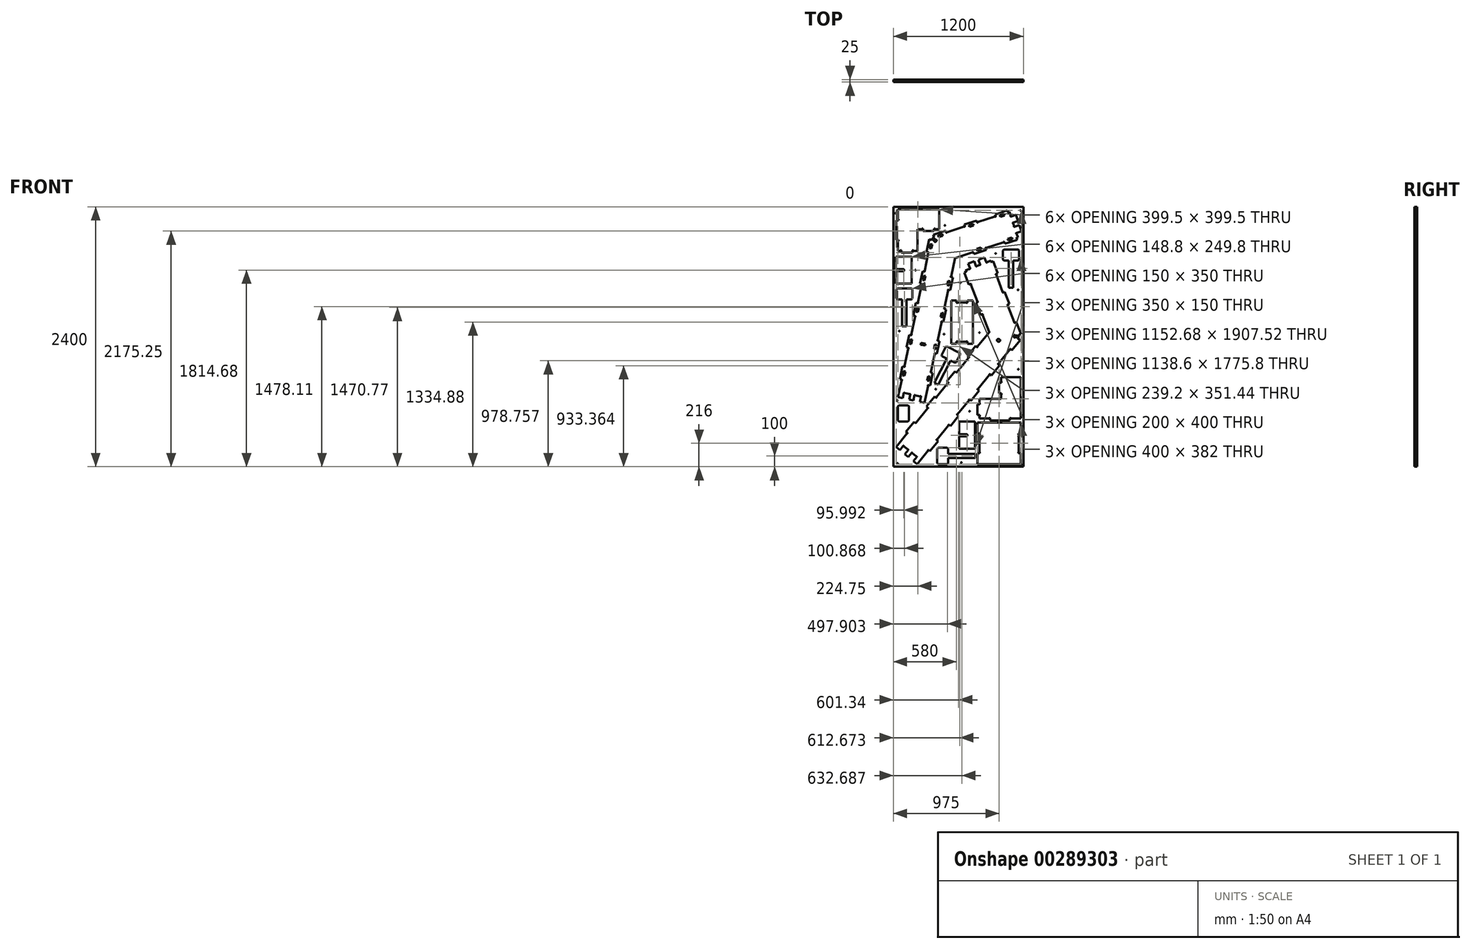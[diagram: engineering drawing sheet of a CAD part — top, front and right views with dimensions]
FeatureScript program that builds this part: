
annotation { "Feature Type Name" : "Feature", "Feature Type Description" : "" }
export const myFeature = defineFeature(function(context is Context, id is Id, definition is map)
    precondition{}
    {
        {
            var Q0;
            Q0=qCreatedBy(makeId("Front.planeOp"),FACE);
            var sketch = newSketch(context, id + "F0", { "sketchPlane" : qUnion([Q0])});
            skLineSegment(sketch, "E0", {"start": v(-600, -1200) * mm, "end": v(600, -1200) * mm});
            skLineSegment(sketch, "E1", {"start": v(600, -1200) * mm, "end": v(600, 1200) * mm});
            skLineSegment(sketch, "E2", {"start": v(600, 1200) * mm, "end": v(-600, 1200) * mm});
            skLineSegment(sketch, "E3", {"start": v(-600, 1200) * mm, "end": v(-600, -1200) * mm});
            skLineSegment(sketch, "E4", {"start": v(-525, 775.5) * mm, "end": v(-525, 798.5) * mm});
            skLineSegment(sketch, "E5", {"start": v(-525, 798.5) * mm, "end": v(-535.5, 798.5) * mm});
            skLineSegment(sketch, "E6", {"start": v(-535.5, 798.5) * mm, "end": v(-535.5, 793.5) * mm});
            skLineSegment(sketch, "E7", {"start": v(-535.5, 793.5) * mm, "end": v(-557, 793.5) * mm});
            skLineSegment(sketch, "E8", {"start": v(-557, 793.5) * mm, "end": v(-557, 883) * mm});
            skLineSegment(sketch, "E9", {"start": v(-557, 883) * mm, "end": v(-552, 883) * mm});
            skLineSegment(sketch, "E10", {"start": v(-552, 883) * mm, "end": v(-552, 893.5) * mm});
            skLineSegment(sketch, "E11", {"start": v(-552, 893.5) * mm, "end": v(-575, 893.5) * mm});
            skLineSegment(sketch, "E12", {"start": v(-575, 893.5) * mm, "end": v(-575, 1075) * mm});
            skLineSegment(sketch, "E13", {"start": v(-575, 1075) * mm, "end": v(-552, 1075) * mm});
            skLineSegment(sketch, "E14", {"start": v(-552, 1075) * mm, "end": v(-552, 1085.5) * mm});
            skLineSegment(sketch, "E15", {"start": v(-552, 1085.5) * mm, "end": v(-557, 1085.5) * mm});
            skLineSegment(sketch, "E16", {"start": v(-557, 1085.5) * mm, "end": v(-557, 1175) * mm});
            skLineSegment(sketch, "E17", {"start": v(-557, 1175) * mm, "end": v(-175.5, 1175) * mm});
            skLineSegment(sketch, "E18", {"start": v(-175.5, 1175) * mm, "end": v(-175.5, 993.5) * mm});
            skLineSegment(sketch, "E19", {"start": v(-175.5, 993.5) * mm, "end": v(-215, 993.5) * mm});
            skLineSegment(sketch, "E20", {"start": v(-215, 993.5) * mm, "end": v(-215, 998.5) * mm});
            skLineSegment(sketch, "E21", {"start": v(-215, 998.5) * mm, "end": v(-225.5, 998.5) * mm});
            skLineSegment(sketch, "E22", {"start": v(-225.5, 998.5) * mm, "end": v(-225.5, 975.5) * mm});
            skLineSegment(sketch, "E23", {"start": v(-225.5, 975.5) * mm, "end": v(-325, 975.5) * mm});
            skLineSegment(sketch, "E24", {"start": v(-325, 975.5) * mm, "end": v(-325, 998.5) * mm});
            skLineSegment(sketch, "E25", {"start": v(-325, 998.5) * mm, "end": v(-335.5, 998.5) * mm});
            skLineSegment(sketch, "E26", {"start": v(-335.5, 998.5) * mm, "end": v(-335.5, 993.5) * mm});
            skLineSegment(sketch, "E27", {"start": v(-335.5, 993.5) * mm, "end": v(-375.5, 993.5) * mm});
            skLineSegment(sketch, "E28", {"start": v(-375.5, 993.5) * mm, "end": v(-375.5, 793.5) * mm});
            skLineSegment(sketch, "E29", {"start": v(-375.5, 793.5) * mm, "end": v(-415, 793.5) * mm});
            skLineSegment(sketch, "E30", {"start": v(-415, 793.5) * mm, "end": v(-415, 798.5) * mm});
            skLineSegment(sketch, "E31", {"start": v(-415, 798.5) * mm, "end": v(-425.5, 798.5) * mm});
            skLineSegment(sketch, "E32", {"start": v(-425.5, 798.5) * mm, "end": v(-425.5, 775.5) * mm});
            skLineSegment(sketch, "E33", {"start": v(-425.5, 775.5) * mm, "end": v(-525, 775.5) * mm});
            skLineSegment(sketch, "E34", {"start": v(175, -723) * mm, "end": v(198, -723) * mm});
            skLineSegment(sketch, "E35", {"start": v(198, -723) * mm, "end": v(198, -733.5) * mm});
            skLineSegment(sketch, "E36", {"start": v(198, -733.5) * mm, "end": v(193, -733.5) * mm});
            skLineSegment(sketch, "E37", {"start": v(193, -733.5) * mm, "end": v(193, -755) * mm});
            skLineSegment(sketch, "E38", {"start": v(193, -755) * mm, "end": v(282.5, -755) * mm});
            skLineSegment(sketch, "E39", {"start": v(282.5, -755) * mm, "end": v(282.5, -750) * mm});
            skLineSegment(sketch, "E40", {"start": v(282.5, -750) * mm, "end": v(293, -750) * mm});
            skLineSegment(sketch, "E41", {"start": v(293, -750) * mm, "end": v(293, -773) * mm});
            skLineSegment(sketch, "E42", {"start": v(293, -773) * mm, "end": v(474.5, -773) * mm});
            skLineSegment(sketch, "E43", {"start": v(474.5, -773) * mm, "end": v(474.5, -750) * mm});
            skLineSegment(sketch, "E44", {"start": v(474.5, -750) * mm, "end": v(485, -750) * mm});
            skLineSegment(sketch, "E45", {"start": v(485, -750) * mm, "end": v(485, -755) * mm});
            skLineSegment(sketch, "E46", {"start": v(485, -755) * mm, "end": v(574.5, -755) * mm});
            skLineSegment(sketch, "E47", {"start": v(574.5, -755) * mm, "end": v(574.5, -373.5) * mm});
            skLineSegment(sketch, "E48", {"start": v(574.5, -373.5) * mm, "end": v(393, -373.5) * mm});
            skLineSegment(sketch, "E49", {"start": v(393, -373.5) * mm, "end": v(393, -413) * mm});
            skLineSegment(sketch, "E50", {"start": v(393, -413) * mm, "end": v(398, -413) * mm});
            skLineSegment(sketch, "E51", {"start": v(398, -413) * mm, "end": v(398, -423.5) * mm});
            skLineSegment(sketch, "E52", {"start": v(398, -423.5) * mm, "end": v(375, -423.5) * mm});
            skLineSegment(sketch, "E53", {"start": v(375, -423.5) * mm, "end": v(375, -523) * mm});
            skLineSegment(sketch, "E54", {"start": v(375, -523) * mm, "end": v(398, -523) * mm});
            skLineSegment(sketch, "E55", {"start": v(398, -523) * mm, "end": v(398, -533.5) * mm});
            skLineSegment(sketch, "E56", {"start": v(398, -533.5) * mm, "end": v(393, -533.5) * mm});
            skLineSegment(sketch, "E57", {"start": v(393, -533.5) * mm, "end": v(393, -573.5) * mm});
            skLineSegment(sketch, "E58", {"start": v(393, -573.5) * mm, "end": v(193, -573.5) * mm});
            skLineSegment(sketch, "E59", {"start": v(193, -573.5) * mm, "end": v(193, -613) * mm});
            skLineSegment(sketch, "E60", {"start": v(193, -613) * mm, "end": v(198, -613) * mm});
            skLineSegment(sketch, "E61", {"start": v(198, -613) * mm, "end": v(198, -623.5) * mm});
            skLineSegment(sketch, "E62", {"start": v(198, -623.5) * mm, "end": v(175, -623.5) * mm});
            skLineSegment(sketch, "E63", {"start": v(175, -623.5) * mm, "end": v(175, -723) * mm});
            skLineSegment(sketch, "E64", {"start": v(557, -903) * mm, "end": v(552, -903) * mm});
            skLineSegment(sketch, "E65", {"start": v(552, -903) * mm, "end": v(552, -893) * mm});
            skLineSegment(sketch, "E66", {"start": v(552, -893) * mm, "end": v(575, -893) * mm});
            skLineSegment(sketch, "E67", {"start": v(575, -893) * mm, "end": v(575, -793) * mm});
            skLineSegment(sketch, "E68", {"start": v(575, -793) * mm, "end": v(175, -793) * mm});
            skLineSegment(sketch, "E69", {"start": v(175, -793) * mm, "end": v(175, -893) * mm});
            skLineSegment(sketch, "E70", {"start": v(175, -893) * mm, "end": v(198, -893) * mm});
            skLineSegment(sketch, "E71", {"start": v(198, -893) * mm, "end": v(198, -903) * mm});
            skLineSegment(sketch, "E72", {"start": v(198, -903) * mm, "end": v(193, -903) * mm});
            skLineSegment(sketch, "E73", {"start": v(193, -903) * mm, "end": v(193, -1065) * mm});
            skLineSegment(sketch, "E74", {"start": v(193, -1065) * mm, "end": v(198, -1065) * mm});
            skLineSegment(sketch, "E75", {"start": v(198, -1065) * mm, "end": v(198, -1075) * mm});
            skLineSegment(sketch, "E76", {"start": v(198, -1075) * mm, "end": v(175, -1075) * mm});
            skLineSegment(sketch, "E77", {"start": v(175, -1075) * mm, "end": v(175, -1175) * mm});
            skLineSegment(sketch, "E78", {"start": v(175, -1175) * mm, "end": v(575, -1175) * mm});
            skLineSegment(sketch, "E79", {"start": v(575, -1175) * mm, "end": v(575, -1075) * mm});
            skLineSegment(sketch, "E80", {"start": v(575, -1075) * mm, "end": v(552, -1075) * mm});
            skLineSegment(sketch, "E81", {"start": v(552, -1075) * mm, "end": v(552, -1065) * mm});
            skLineSegment(sketch, "E82", {"start": v(552, -1065) * mm, "end": v(557, -1065) * mm});
            skLineSegment(sketch, "E83", {"start": v(557, -1065) * mm, "end": v(557, -903) * mm});
            skLineSegment(sketch, "E84", {"start": v(132.69, 334.88) * mm, "end": v(82.69, 334.88) * mm});
            skLineSegment(sketch, "E85", {"start": v(82.69, 334.88) * mm, "end": v(82.69, 311.88) * mm});
            skLineSegment(sketch, "E86", {"start": v(82.69, 311.88) * mm, "end": v(72.69, 311.88) * mm});
            skLineSegment(sketch, "E87", {"start": v(72.69, 311.88) * mm, "end": v(72.69, 316.88) * mm});
            skLineSegment(sketch, "E88", {"start": v(72.69, 316.88) * mm, "end": v(-7.31, 316.88) * mm});
            skLineSegment(sketch, "E89", {"start": v(-7.31, 316.88) * mm, "end": v(-7.31, 311.88) * mm});
            skLineSegment(sketch, "E90", {"start": v(-7.31, 311.88) * mm, "end": v(-17.31, 311.88) * mm});
            skLineSegment(sketch, "E91", {"start": v(-17.31, 311.88) * mm, "end": v(-17.31, 334.88) * mm});
            skLineSegment(sketch, "E92", {"start": v(-17.31, 334.88) * mm, "end": v(-67.31, 334.88) * mm});
            skLineSegment(sketch, "E93", {"start": v(-67.31, 334.88) * mm, "end": v(-67.31, -65.12) * mm});
            skLineSegment(sketch, "E94", {"start": v(-67.31, -65.12) * mm, "end": v(-17.31, -65.12) * mm});
            skLineSegment(sketch, "E95", {"start": v(-17.31, -65.12) * mm, "end": v(-17.31, -42.12) * mm});
            skLineSegment(sketch, "E96", {"start": v(-17.31, -42.12) * mm, "end": v(-7.31, -42.12) * mm});
            skLineSegment(sketch, "E97", {"start": v(-7.31, -42.12) * mm, "end": v(-7.31, -47.12) * mm});
            skLineSegment(sketch, "E98", {"start": v(-7.31, -47.12) * mm, "end": v(72.69, -47.12) * mm});
            skLineSegment(sketch, "E99", {"start": v(72.69, -47.12) * mm, "end": v(72.69, -42.12) * mm});
            skLineSegment(sketch, "E100", {"start": v(72.69, -42.12) * mm, "end": v(82.69, -42.12) * mm});
            skLineSegment(sketch, "E101", {"start": v(82.69, -42.12) * mm, "end": v(82.69, -65.12) * mm});
            skLineSegment(sketch, "E102", {"start": v(82.69, -65.12) * mm, "end": v(132.69, -65.12) * mm});
            skLineSegment(sketch, "E103", {"start": v(132.69, -65.12) * mm, "end": v(132.69, 334.88) * mm});
            skLineSegment(sketch, "E104", {"start": v(-479.13, 95.77) * mm, "end": v(-479.13, 345.77) * mm});
            skLineSegment(sketch, "E105", {"start": v(-479.13, 345.77) * mm, "end": v(-432.35, 345.77) * mm});
            skLineSegment(sketch, "E106", {"start": v(-432.35, 345.77) * mm, "end": v(-424.13, 353.99) * mm});
            skLineSegment(sketch, "E107", {"start": v(-424.13, 353.99) * mm, "end": v(-424.13, 437.55) * mm});
            skLineSegment(sketch, "E108", {"start": v(-424.13, 437.55) * mm, "end": v(-432.35, 445.77) * mm});
            skLineSegment(sketch, "E109", {"start": v(-432.35, 445.77) * mm, "end": v(-565.92, 445.77) * mm});
            skLineSegment(sketch, "E110", {"start": v(-565.92, 445.77) * mm, "end": v(-574.13, 437.55) * mm});
            skLineSegment(sketch, "E111", {"start": v(-574.13, 437.55) * mm, "end": v(-574.13, 353.99) * mm});
            skLineSegment(sketch, "E112", {"start": v(-574.13, 353.99) * mm, "end": v(-565.92, 345.77) * mm});
            skLineSegment(sketch, "E113", {"start": v(-565.92, 345.77) * mm, "end": v(-519.13, 345.77) * mm});
            skLineSegment(sketch, "E114", {"start": v(-519.13, 345.77) * mm, "end": v(-519.13, 95.77) * mm});
            skLineSegment(sketch, "E115", {"start": v(-519.13, 95.77) * mm, "end": v(-479.13, 95.77) * mm});
            skLineSegment(sketch, "E116", {"start": v(155, -1120) * mm, "end": v(-95, -1120) * mm});
            skLineSegment(sketch, "E117", {"start": v(-95, -1120) * mm, "end": v(-95, -1166.78) * mm});
            skLineSegment(sketch, "E118", {"start": v(-95, -1166.78) * mm, "end": v(-103.22, -1175) * mm});
            skLineSegment(sketch, "E119", {"start": v(-103.22, -1175) * mm, "end": v(-186.78, -1175) * mm});
            skLineSegment(sketch, "E120", {"start": v(-186.78, -1175) * mm, "end": v(-195, -1166.78) * mm});
            skLineSegment(sketch, "E121", {"start": v(-195, -1166.78) * mm, "end": v(-195, -1033.22) * mm});
            skLineSegment(sketch, "E122", {"start": v(-195, -1033.22) * mm, "end": v(-186.78, -1025) * mm});
            skLineSegment(sketch, "E123", {"start": v(-186.78, -1025) * mm, "end": v(-103.22, -1025) * mm});
            skLineSegment(sketch, "E124", {"start": v(-103.22, -1025) * mm, "end": v(-95, -1033.22) * mm});
            skLineSegment(sketch, "E125", {"start": v(-95, -1033.22) * mm, "end": v(-95, -1080) * mm});
            skLineSegment(sketch, "E126", {"start": v(-95, -1080) * mm, "end": v(155, -1080) * mm});
            skLineSegment(sketch, "E127", {"start": v(155, -1080) * mm, "end": v(155, -1120) * mm});
            skLineSegment(sketch, "E128", {"start": v(505.12, 454.08) * mm, "end": v(505.12, 704.08) * mm});
            skLineSegment(sketch, "E129", {"start": v(505.12, 704.08) * mm, "end": v(551.9, 704.08) * mm});
            skLineSegment(sketch, "E130", {"start": v(551.9, 704.08) * mm, "end": v(560.12, 712.3) * mm});
            skLineSegment(sketch, "E131", {"start": v(560.12, 712.3) * mm, "end": v(560.12, 795.87) * mm});
            skLineSegment(sketch, "E132", {"start": v(560.12, 795.87) * mm, "end": v(551.9, 804.08) * mm});
            skLineSegment(sketch, "E133", {"start": v(551.9, 804.08) * mm, "end": v(418.34, 804.08) * mm});
            skLineSegment(sketch, "E134", {"start": v(418.34, 804.08) * mm, "end": v(410.12, 795.87) * mm});
            skLineSegment(sketch, "E135", {"start": v(410.12, 795.87) * mm, "end": v(410.12, 712.3) * mm});
            skLineSegment(sketch, "E136", {"start": v(410.12, 712.3) * mm, "end": v(418.34, 704.08) * mm});
            skLineSegment(sketch, "E137", {"start": v(418.34, 704.08) * mm, "end": v(465.12, 704.08) * mm});
            skLineSegment(sketch, "E138", {"start": v(465.12, 704.08) * mm, "end": v(465.12, 454.08) * mm});
            skLineSegment(sketch, "E139", {"start": v(465.12, 454.08) * mm, "end": v(505.12, 454.08) * mm});
            skLineSegment(sketch, "E140", {"start": v(-186.02, -442.36) * mm, "end": v(-73.04, -219.34) * mm});
            skLineSegment(sketch, "E141", {"start": v(-73.04, -219.34) * mm, "end": v(-31.3, -240.48) * mm});
            skLineSegment(sketch, "E142", {"start": v(-31.3, -240.48) * mm, "end": v(-20.26, -236.87) * mm});
            skLineSegment(sketch, "E143", {"start": v(-20.26, -236.87) * mm, "end": v(17.5, -162.32) * mm});
            skLineSegment(sketch, "E144", {"start": v(17.5, -162.32) * mm, "end": v(13.89, -151.28) * mm});
            skLineSegment(sketch, "E145", {"start": v(13.89, -151.28) * mm, "end": v(-105.26, -90.92) * mm});
            skLineSegment(sketch, "E146", {"start": v(-105.26, -90.92) * mm, "end": v(-116.3, -94.53) * mm});
            skLineSegment(sketch, "E147", {"start": v(-116.3, -94.53) * mm, "end": v(-154.07, -169.08) * mm});
            skLineSegment(sketch, "E148", {"start": v(-154.07, -169.08) * mm, "end": v(-150.46, -180.12) * mm});
            skLineSegment(sketch, "E149", {"start": v(-150.46, -180.12) * mm, "end": v(-108.72, -201.26) * mm});
            skLineSegment(sketch, "E150", {"start": v(-108.72, -201.26) * mm, "end": v(-221.7, -424.28) * mm});
            skLineSegment(sketch, "E151", {"start": v(-221.7, -424.28) * mm, "end": v(-186.02, -442.36) * mm});
            skLineSegment(sketch, "E152", {"start": v(-557.7, -773.81) * mm, "end": v(-549.49, -782.03) * mm});
            skLineSegment(sketch, "E153", {"start": v(-549.49, -782.03) * mm, "end": v(-465.92, -782.03) * mm});
            skLineSegment(sketch, "E154", {"start": v(-465.92, -782.03) * mm, "end": v(-457.7, -773.81) * mm});
            skLineSegment(sketch, "E155", {"start": v(-457.7, -773.81) * mm, "end": v(-457.7, -640.25) * mm});
            skLineSegment(sketch, "E156", {"start": v(-457.7, -640.25) * mm, "end": v(-465.92, -632.03) * mm});
            skLineSegment(sketch, "E157", {"start": v(-465.92, -632.03) * mm, "end": v(-549.49, -632.03) * mm});
            skLineSegment(sketch, "E158", {"start": v(-549.49, -632.03) * mm, "end": v(-557.7, -640.25) * mm});
            skLineSegment(sketch, "E159", {"start": v(-557.7, -640.25) * mm, "end": v(-557.7, -773.81) * mm});
            skArc(sketch, "E160", {"start": v(348.52, 571.82) * mm, "mid": v(344.5, 573.9) * mm, "end": v(346.42, 578) * mm});
            skLineSegment(sketch, "E161", {"start": v(346.42, 578) * mm, "end": v(363, 584.35) * mm});
            skLineSegment(sketch, "E162", {"start": v(363, 584.35) * mm, "end": v(320.24, 695.94) * mm});
            skLineSegment(sketch, "E163", {"start": v(320.24, 695.94) * mm, "end": v(303.67, 689.6) * mm});
            skArc(sketch, "E164", {"start": v(303.67, 689.6) * mm, "mid": v(299.5, 691.36) * mm, "end": v(301.1, 695.59) * mm});
            skLineSegment(sketch, "E165", {"start": v(301.1, 695.59) * mm, "end": v(298.67, 701.93) * mm});
            skLineSegment(sketch, "E166", {"start": v(298.67, 701.93) * mm, "end": v(262.74, 688.16) * mm});
            skArc(sketch, "E167", {"start": v(262.74, 688.16) * mm, "mid": v(260.66, 684.13) * mm, "end": v(256.56, 686.06) * mm});
            skLineSegment(sketch, "E168", {"start": v(256.56, 686.06) * mm, "end": v(238.76, 732.52) * mm});
            skLineSegment(sketch, "E169", {"start": v(238.76, 732.52) * mm, "end": v(183.2, 711.23) * mm});
            skLineSegment(sketch, "E170", {"start": v(183.2, 711.23) * mm, "end": v(201, 664.77) * mm});
            skArc(sketch, "E171", {"start": v(201, 664.77) * mm, "mid": v(199.23, 660.6) * mm, "end": v(195, 662.2) * mm});
            skLineSegment(sketch, "E172", {"start": v(195, 662.2) * mm, "end": v(169.36, 652.38) * mm});
            skArc(sketch, "E173", {"start": v(169.36, 652.38) * mm, "mid": v(167.28, 648.35) * mm, "end": v(163.18, 650.28) * mm});
            skLineSegment(sketch, "E174", {"start": v(163.18, 650.28) * mm, "end": v(145.38, 696.73) * mm});
            skLineSegment(sketch, "E175", {"start": v(145.38, 696.73) * mm, "end": v(89.82, 675.45) * mm});
            skLineSegment(sketch, "E176", {"start": v(89.82, 675.45) * mm, "end": v(107.62, 628.99) * mm});
            skArc(sketch, "E177", {"start": v(107.62, 628.99) * mm, "mid": v(105.86, 624.82) * mm, "end": v(101.62, 626.42) * mm});
            skLineSegment(sketch, "E178", {"start": v(101.62, 626.42) * mm, "end": v(65.69, 612.65) * mm});
            skLineSegment(sketch, "E179", {"start": v(65.69, 612.65) * mm, "end": v(68.12, 606.32) * mm});
            skArc(sketch, "E180", {"start": v(68.12, 606.32) * mm, "mid": v(72.14, 604.24) * mm, "end": v(70.22, 600.14) * mm});
            skLineSegment(sketch, "E181", {"start": v(70.22, 600.14) * mm, "end": v(53.64, 593.79) * mm});
            skLineSegment(sketch, "E182", {"start": v(53.64, 593.79) * mm, "end": v(96.4, 482.2) * mm});
            skLineSegment(sketch, "E183", {"start": v(96.4, 482.2) * mm, "end": v(112.97, 488.55) * mm});
            skArc(sketch, "E184", {"start": v(112.97, 488.55) * mm, "mid": v(117.14, 486.79) * mm, "end": v(115.54, 482.55) * mm});
            skLineSegment(sketch, "E185", {"start": v(115.54, 482.55) * mm, "end": v(175.46, 326.18) * mm});
            skArc(sketch, "E186", {"start": v(175.46, 326.18) * mm, "mid": v(179.49, 324.1) * mm, "end": v(177.56, 320) * mm});
            skLineSegment(sketch, "E187", {"start": v(177.56, 320) * mm, "end": v(160.98, 313.65) * mm});
            skLineSegment(sketch, "E188", {"start": v(160.98, 313.65) * mm, "end": v(203.74, 202.06) * mm});
            skLineSegment(sketch, "E189", {"start": v(203.74, 202.06) * mm, "end": v(220.32, 208.41) * mm});
            skArc(sketch, "E190", {"start": v(220.32, 208.41) * mm, "mid": v(224.48, 206.65) * mm, "end": v(222.88, 202.41) * mm});
            skLineSegment(sketch, "E191", {"start": v(222.88, 202.41) * mm, "end": v(283, 45.53) * mm});
            skArc(sketch, "E192", {"start": v(283, 45.53) * mm, "mid": v(285.56, 41.82) * mm, "end": v(281.97, 39.1) * mm});
            skLineSegment(sketch, "E193", {"start": v(281.97, 39.1) * mm, "end": v(176.16, -91.4) * mm});
            skArc(sketch, "E194", {"start": v(176.16, -91.4) * mm, "mid": v(176.38, -95.93) * mm, "end": v(171.86, -96.31) * mm});
            skLineSegment(sketch, "E195", {"start": v(171.86, -96.31) * mm, "end": v(158.08, -85.13) * mm});
            skLineSegment(sketch, "E196", {"start": v(158.08, -85.13) * mm, "end": v(82.82, -177.96) * mm});
            skLineSegment(sketch, "E197", {"start": v(82.82, -177.96) * mm, "end": v(96.6, -189.14) * mm});
            skArc(sketch, "E198", {"start": v(96.6, -189.14) * mm, "mid": v(97.16, -193.63) * mm, "end": v(92.7, -194.36) * mm});
            skLineSegment(sketch, "E199", {"start": v(92.7, -194.36) * mm, "end": v(-12.77, -324.44) * mm});
            skArc(sketch, "E200", {"start": v(-12.77, -324.44) * mm, "mid": v(-12.56, -328.96) * mm, "end": v(-17.07, -329.34) * mm});
            skLineSegment(sketch, "E201", {"start": v(-17.07, -329.34) * mm, "end": v(-30.86, -318.16) * mm});
            skLineSegment(sketch, "E202", {"start": v(-30.86, -318.16) * mm, "end": v(-106.12, -410.99) * mm});
            skLineSegment(sketch, "E203", {"start": v(-106.12, -410.99) * mm, "end": v(-92.33, -422.17) * mm});
            skArc(sketch, "E204", {"start": v(-92.33, -422.17) * mm, "mid": v(-91.78, -426.66) * mm, "end": v(-96.25, -427.39) * mm});
            skLineSegment(sketch, "E205", {"start": v(-96.25, -427.39) * mm, "end": v(-201.71, -557.47) * mm});
            skArc(sketch, "E206", {"start": v(-201.71, -557.47) * mm, "mid": v(-201.5, -562) * mm, "end": v(-206.01, -562.37) * mm});
            skLineSegment(sketch, "E207", {"start": v(-206.01, -562.37) * mm, "end": v(-219.8, -551.2) * mm});
            skLineSegment(sketch, "E208", {"start": v(-219.8, -551.2) * mm, "end": v(-295.06, -644.02) * mm});
            skLineSegment(sketch, "E209", {"start": v(-295.06, -644.02) * mm, "end": v(-281.27, -655.2) * mm});
            skArc(sketch, "E210", {"start": v(-281.27, -655.2) * mm, "mid": v(-280.72, -659.69) * mm, "end": v(-285.18, -660.42) * mm});
            skLineSegment(sketch, "E211", {"start": v(-285.18, -660.42) * mm, "end": v(-390.65, -790.5) * mm});
            skArc(sketch, "E212", {"start": v(-390.65, -790.5) * mm, "mid": v(-390.43, -795.02) * mm, "end": v(-394.95, -795.4) * mm});
            skLineSegment(sketch, "E213", {"start": v(-394.95, -795.4) * mm, "end": v(-408.74, -784.22) * mm});
            skLineSegment(sketch, "E214", {"start": v(-408.74, -784.22) * mm, "end": v(-484, -877.05) * mm});
            skLineSegment(sketch, "E215", {"start": v(-484, -877.05) * mm, "end": v(-470.2, -888.23) * mm});
            skArc(sketch, "E216", {"start": v(-470.2, -888.23) * mm, "mid": v(-469.66, -892.72) * mm, "end": v(-474.12, -893.45) * mm});
            skLineSegment(sketch, "E217", {"start": v(-474.12, -893.45) * mm, "end": v(-575, -1017.87) * mm});
            skLineSegment(sketch, "E218", {"start": v(-575, -1017.87) * mm, "end": v(-540.43, -1045.9) * mm});
            skLineSegment(sketch, "E219", {"start": v(-540.43, -1045.9) * mm, "end": v(-509.1, -1007.25) * mm});
            skArc(sketch, "E220", {"start": v(-509.1, -1007.25) * mm, "mid": v(-504.61, -1006.7) * mm, "end": v(-503.88, -1011.16) * mm});
            skLineSegment(sketch, "E221", {"start": v(-503.88, -1011.16) * mm, "end": v(-467.01, -1041.05) * mm});
            skArc(sketch, "E222", {"start": v(-467.01, -1041.05) * mm, "mid": v(-462.49, -1040.84) * mm, "end": v(-462.1, -1045.35) * mm});
            skLineSegment(sketch, "E223", {"start": v(-462.1, -1045.35) * mm, "end": v(-493.44, -1084) * mm});
            skLineSegment(sketch, "E224", {"start": v(-493.44, -1084) * mm, "end": v(-462.76, -1108.87) * mm});
            skLineSegment(sketch, "E225", {"start": v(-462.76, -1108.87) * mm, "end": v(-431.43, -1070.23) * mm});
            skArc(sketch, "E226", {"start": v(-431.43, -1070.23) * mm, "mid": v(-426.93, -1069.67) * mm, "end": v(-426.2, -1074.14) * mm});
            skLineSegment(sketch, "E227", {"start": v(-426.2, -1074.14) * mm, "end": v(-389.34, -1104.03) * mm});
            skArc(sketch, "E228", {"start": v(-389.34, -1104.03) * mm, "mid": v(-384.81, -1103.82) * mm, "end": v(-384.43, -1108.33) * mm});
            skLineSegment(sketch, "E229", {"start": v(-384.43, -1108.33) * mm, "end": v(-415.76, -1146.97) * mm});
            skLineSegment(sketch, "E230", {"start": v(-415.76, -1146.97) * mm, "end": v(-381.2, -1175) * mm});
            skLineSegment(sketch, "E231", {"start": v(-381.2, -1175) * mm, "end": v(-280.32, -1050.58) * mm});
            skArc(sketch, "E232", {"start": v(-280.32, -1050.58) * mm, "mid": v(-280.53, -1046.05) * mm, "end": v(-276.02, -1045.67) * mm});
            skLineSegment(sketch, "E233", {"start": v(-276.02, -1045.67) * mm, "end": v(-262.23, -1056.85) * mm});
            skLineSegment(sketch, "E234", {"start": v(-262.23, -1056.85) * mm, "end": v(-186.97, -964.03) * mm});
            skLineSegment(sketch, "E235", {"start": v(-186.97, -964.03) * mm, "end": v(-200.76, -952.85) * mm});
            skArc(sketch, "E236", {"start": v(-200.76, -952.85) * mm, "mid": v(-201.31, -948.36) * mm, "end": v(-196.85, -947.63) * mm});
            skLineSegment(sketch, "E237", {"start": v(-196.85, -947.63) * mm, "end": v(-91.38, -817.55) * mm});
            skArc(sketch, "E238", {"start": v(-91.38, -817.55) * mm, "mid": v(-91.6, -813.03) * mm, "end": v(-87.08, -812.64) * mm});
            skLineSegment(sketch, "E239", {"start": v(-87.08, -812.64) * mm, "end": v(-73.3, -823.82) * mm});
            skLineSegment(sketch, "E240", {"start": v(-73.3, -823.82) * mm, "end": v(1.97, -731) * mm});
            skLineSegment(sketch, "E241", {"start": v(1.97, -731) * mm, "end": v(-11.82, -719.82) * mm});
            skArc(sketch, "E242", {"start": v(-11.82, -719.82) * mm, "mid": v(-12.37, -715.33) * mm, "end": v(-7.9, -714.6) * mm});
            skLineSegment(sketch, "E243", {"start": v(-7.9, -714.6) * mm, "end": v(97.56, -584.52) * mm});
            skArc(sketch, "E244", {"start": v(97.56, -584.52) * mm, "mid": v(97.34, -580) * mm, "end": v(101.86, -579.61) * mm});
            skLineSegment(sketch, "E245", {"start": v(101.86, -579.61) * mm, "end": v(115.64, -590.8) * mm});
            skLineSegment(sketch, "E246", {"start": v(115.64, -590.8) * mm, "end": v(190.9, -497.97) * mm});
            skLineSegment(sketch, "E247", {"start": v(190.9, -497.97) * mm, "end": v(177.12, -486.8) * mm});
            skArc(sketch, "E248", {"start": v(177.12, -486.8) * mm, "mid": v(176.56, -482.3) * mm, "end": v(181.03, -481.57) * mm});
            skLineSegment(sketch, "E249", {"start": v(181.03, -481.57) * mm, "end": v(286.5, -351.5) * mm});
            skArc(sketch, "E250", {"start": v(286.5, -351.5) * mm, "mid": v(286.28, -346.97) * mm, "end": v(290.8, -346.59) * mm});
            skLineSegment(sketch, "E251", {"start": v(290.8, -346.59) * mm, "end": v(304.58, -357.76) * mm});
            skLineSegment(sketch, "E252", {"start": v(304.58, -357.76) * mm, "end": v(379.84, -264.94) * mm});
            skLineSegment(sketch, "E253", {"start": v(379.84, -264.94) * mm, "end": v(366.05, -253.76) * mm});
            skArc(sketch, "E254", {"start": v(366.05, -253.76) * mm, "mid": v(365.5, -249.27) * mm, "end": v(369.97, -248.54) * mm});
            skLineSegment(sketch, "E255", {"start": v(369.97, -248.54) * mm, "end": v(475.43, -118.46) * mm});
            skArc(sketch, "E256", {"start": v(475.43, -118.46) * mm, "mid": v(475.22, -113.94) * mm, "end": v(479.73, -113.56) * mm});
            skLineSegment(sketch, "E257", {"start": v(479.73, -113.56) * mm, "end": v(493.52, -124.73) * mm});
            skLineSegment(sketch, "E258", {"start": v(493.52, -124.73) * mm, "end": v(568.78, -31.91) * mm});
            skLineSegment(sketch, "E259", {"start": v(568.78, -31.91) * mm, "end": v(559.86, -24.68) * mm});
            skArc(sketch, "E260", {"start": v(559.86, -24.68) * mm, "mid": v(555.34, -24.9) * mm, "end": v(554.96, -20.38) * mm});
            skLineSegment(sketch, "E261", {"start": v(554.96, -20.38) * mm, "end": v(562.14, -11.52) * mm});
            skLineSegment(sketch, "E262", {"start": v(562.14, -11.52) * mm, "end": v(519.38, -4.72) * mm});
            skArc(sketch, "E263", {"start": v(519.38, -4.72) * mm, "mid": v(515.57, -7.17) * mm, "end": v(512.98, -3.45) * mm});
            skLineSegment(sketch, "E264", {"start": v(512.98, -3.45) * mm, "end": v(515.8, 14.32) * mm});
            skArc(sketch, "E265", {"start": v(515.8, 14.32) * mm, "mid": v(519.42, 17.05) * mm, "end": v(522.28, 13.55) * mm});
            skLineSegment(sketch, "E266", {"start": v(522.28, 13.55) * mm, "end": v(565.04, 6.75) * mm});
            skLineSegment(sketch, "E267", {"start": v(565.04, 6.75) * mm, "end": v(560.96, 17.4) * mm});
            skArc(sketch, "E268", {"start": v(560.96, 17.4) * mm, "mid": v(562.73, 21.57) * mm, "end": v(566.96, 19.97) * mm});
            skLineSegment(sketch, "E269", {"start": v(566.96, 19.97) * mm, "end": v(577.68, 24.07) * mm});
            skLineSegment(sketch, "E270", {"start": v(577.68, 24.07) * mm, "end": v(534.92, 135.66) * mm});
            skLineSegment(sketch, "E271", {"start": v(534.92, 135.66) * mm, "end": v(518.35, 129.31) * mm});
            skArc(sketch, "E272", {"start": v(518.35, 129.31) * mm, "mid": v(514.18, 131.08) * mm, "end": v(515.78, 135.31) * mm});
            skLineSegment(sketch, "E273", {"start": v(515.78, 135.31) * mm, "end": v(455.86, 291.68) * mm});
            skArc(sketch, "E274", {"start": v(455.86, 291.68) * mm, "mid": v(451.84, 293.76) * mm, "end": v(453.77, 297.86) * mm});
            skLineSegment(sketch, "E275", {"start": v(453.77, 297.86) * mm, "end": v(470.34, 304.21) * mm});
            skLineSegment(sketch, "E276", {"start": v(470.34, 304.21) * mm, "end": v(427.58, 415.8) * mm});
            skLineSegment(sketch, "E277", {"start": v(427.58, 415.8) * mm, "end": v(411, 409.45) * mm});
            skArc(sketch, "E278", {"start": v(411, 409.45) * mm, "mid": v(406.84, 411.22) * mm, "end": v(408.44, 415.45) * mm});
            skLineSegment(sketch, "E279", {"start": v(408.44, 415.45) * mm, "end": v(348.52, 571.82) * mm});
            skLineSegment(sketch, "E280", {"start": v(422.35, 874.36) * mm, "end": v(427.88, 857.49) * mm});
            skLineSegment(sketch, "E281", {"start": v(427.88, 857.49) * mm, "end": v(541.44, 894.71) * mm});
            skLineSegment(sketch, "E282", {"start": v(541.44, 894.71) * mm, "end": v(535.9, 911.58) * mm});
            skArc(sketch, "E283", {"start": v(535.9, 911.58) * mm, "mid": v(537.88, 915.65) * mm, "end": v(542.03, 913.85) * mm});
            skLineSegment(sketch, "E284", {"start": v(542.03, 913.85) * mm, "end": v(548.48, 915.96) * mm});
            skLineSegment(sketch, "E285", {"start": v(548.48, 915.96) * mm, "end": v(536.49, 952.53) * mm});
            skArc(sketch, "E286", {"start": v(536.49, 952.53) * mm, "mid": v(532.57, 954.8) * mm, "end": v(534.7, 958.8) * mm});
            skLineSegment(sketch, "E287", {"start": v(534.7, 958.8) * mm, "end": v(581.97, 974.3) * mm});
            skLineSegment(sketch, "E288", {"start": v(581.97, 974.3) * mm, "end": v(563.44, 1030.84) * mm});
            skLineSegment(sketch, "E289", {"start": v(563.44, 1030.84) * mm, "end": v(516.16, 1015.34) * mm});
            skArc(sketch, "E290", {"start": v(516.16, 1015.34) * mm, "mid": v(512.09, 1017.3) * mm, "end": v(513.9, 1021.46) * mm});
            skLineSegment(sketch, "E291", {"start": v(513.9, 1021.46) * mm, "end": v(505.34, 1047.55) * mm});
            skArc(sketch, "E292", {"start": v(505.34, 1047.55) * mm, "mid": v(501.42, 1049.82) * mm, "end": v(503.55, 1053.82) * mm});
            skLineSegment(sketch, "E293", {"start": v(503.55, 1053.82) * mm, "end": v(550.82, 1069.32) * mm});
            skLineSegment(sketch, "E294", {"start": v(550.82, 1069.32) * mm, "end": v(532.29, 1125.86) * mm});
            skLineSegment(sketch, "E295", {"start": v(532.29, 1125.86) * mm, "end": v(485.01, 1110.37) * mm});
            skArc(sketch, "E296", {"start": v(485.01, 1110.37) * mm, "mid": v(480.94, 1112.33) * mm, "end": v(482.75, 1116.48) * mm});
            skLineSegment(sketch, "E297", {"start": v(482.75, 1116.48) * mm, "end": v(470.76, 1153.05) * mm});
            skLineSegment(sketch, "E298", {"start": v(470.76, 1153.05) * mm, "end": v(464.31, 1150.94) * mm});
            skArc(sketch, "E299", {"start": v(464.31, 1150.94) * mm, "mid": v(462.04, 1147.02) * mm, "end": v(458.04, 1149.14) * mm});
            skLineSegment(sketch, "E300", {"start": v(458.04, 1149.14) * mm, "end": v(452.5, 1166) * mm});
            skLineSegment(sketch, "E301", {"start": v(452.5, 1166) * mm, "end": v(338.95, 1128.79) * mm});
            skLineSegment(sketch, "E302", {"start": v(338.95, 1128.79) * mm, "end": v(344.48, 1111.92) * mm});
            skArc(sketch, "E303", {"start": v(344.48, 1111.92) * mm, "mid": v(342.51, 1107.85) * mm, "end": v(338.36, 1109.65) * mm});
            skLineSegment(sketch, "E304", {"start": v(338.36, 1109.65) * mm, "end": v(179.24, 1057.49) * mm});
            skArc(sketch, "E305", {"start": v(179.24, 1057.49) * mm, "mid": v(176.96, 1053.57) * mm, "end": v(172.96, 1055.7) * mm});
            skLineSegment(sketch, "E306", {"start": v(172.96, 1055.7) * mm, "end": v(167.43, 1072.56) * mm});
            skLineSegment(sketch, "E307", {"start": v(167.43, 1072.56) * mm, "end": v(53.88, 1035.34) * mm});
            skLineSegment(sketch, "E308", {"start": v(53.88, 1035.34) * mm, "end": v(59.4, 1018.47) * mm});
            skArc(sketch, "E309", {"start": v(59.4, 1018.47) * mm, "mid": v(57.44, 1014.4) * mm, "end": v(53.29, 1016.2) * mm});
            skLineSegment(sketch, "E310", {"start": v(53.29, 1016.2) * mm, "end": v(-105.84, 964.04) * mm});
            skArc(sketch, "E311", {"start": v(-105.84, 964.04) * mm, "mid": v(-108.11, 960.12) * mm, "end": v(-112.11, 962.25) * mm});
            skLineSegment(sketch, "E312", {"start": v(-112.11, 962.25) * mm, "end": v(-117.64, 979.12) * mm});
            skLineSegment(sketch, "E313", {"start": v(-117.64, 979.12) * mm, "end": v(-231.2, 941.9) * mm});
            skLineSegment(sketch, "E314", {"start": v(-231.2, 941.9) * mm, "end": v(-227.62, 930.99) * mm});
            skArc(sketch, "E315", {"start": v(-227.62, 930.99) * mm, "mid": v(-223.7, 928.71) * mm, "end": v(-225.83, 924.71) * mm});
            skLineSegment(sketch, "E316", {"start": v(-225.83, 924.71) * mm, "end": v(-236.67, 921.16) * mm});
            skLineSegment(sketch, "E317", {"start": v(-236.67, 921.16) * mm, "end": v(-204.42, 892.27) * mm});
            skArc(sketch, "E318", {"start": v(-204.42, 892.27) * mm, "mid": v(-199.89, 892.26) * mm, "end": v(-199.73, 887.73) * mm});
            skLineSegment(sketch, "E319", {"start": v(-199.73, 887.73) * mm, "end": v(-211.74, 874.33) * mm});
            skArc(sketch, "E320", {"start": v(-211.74, 874.33) * mm, "mid": v(-216.25, 874) * mm, "end": v(-216.76, 878.5) * mm});
            skLineSegment(sketch, "E321", {"start": v(-216.76, 878.5) * mm, "end": v(-249.01, 907.38) * mm});
            skLineSegment(sketch, "E322", {"start": v(-249.01, 907.38) * mm, "end": v(-251.35, 896.22) * mm});
            skArc(sketch, "E323", {"start": v(-251.35, 896.22) * mm, "mid": v(-255.1, 893.67) * mm, "end": v(-257.79, 897.31) * mm});
            skLineSegment(sketch, "E324", {"start": v(-257.79, 897.31) * mm, "end": v(-269.02, 899.67) * mm});
            skLineSegment(sketch, "E325", {"start": v(-269.02, 899.67) * mm, "end": v(-293.56, 782.72) * mm});
            skLineSegment(sketch, "E326", {"start": v(-293.56, 782.72) * mm, "end": v(-276.2, 779.07) * mm});
            skArc(sketch, "E327", {"start": v(-276.2, 779.07) * mm, "mid": v(-273.65, 775.33) * mm, "end": v(-277.29, 772.64) * mm});
            skLineSegment(sketch, "E328", {"start": v(-277.29, 772.64) * mm, "end": v(-311.68, 608.75) * mm});
            skArc(sketch, "E329", {"start": v(-311.68, 608.75) * mm, "mid": v(-309.42, 604.82) * mm, "end": v(-313.26, 602.42) * mm});
            skLineSegment(sketch, "E330", {"start": v(-313.26, 602.42) * mm, "end": v(-330.63, 606.06) * mm});
            skLineSegment(sketch, "E331", {"start": v(-330.63, 606.06) * mm, "end": v(-355.17, 489.11) * mm});
            skLineSegment(sketch, "E332", {"start": v(-355.17, 489.11) * mm, "end": v(-337.8, 485.47) * mm});
            skArc(sketch, "E333", {"start": v(-337.8, 485.47) * mm, "mid": v(-335.26, 481.72) * mm, "end": v(-338.9, 479.03) * mm});
            skLineSegment(sketch, "E334", {"start": v(-338.9, 479.03) * mm, "end": v(-373.29, 315.14) * mm});
            skArc(sketch, "E335", {"start": v(-373.29, 315.14) * mm, "mid": v(-371.03, 311.21) * mm, "end": v(-374.87, 308.81) * mm});
            skLineSegment(sketch, "E336", {"start": v(-374.87, 308.81) * mm, "end": v(-392.24, 312.46) * mm});
            skLineSegment(sketch, "E337", {"start": v(-392.24, 312.46) * mm, "end": v(-416.78, 195.5) * mm});
            skLineSegment(sketch, "E338", {"start": v(-416.78, 195.5) * mm, "end": v(-399.41, 191.86) * mm});
            skArc(sketch, "E339", {"start": v(-399.41, 191.86) * mm, "mid": v(-396.87, 188.12) * mm, "end": v(-400.5, 185.43) * mm});
            skLineSegment(sketch, "E340", {"start": v(-400.5, 185.43) * mm, "end": v(-434.9, 21.54) * mm});
            skArc(sketch, "E341", {"start": v(-434.9, 21.54) * mm, "mid": v(-432.64, 17.6) * mm, "end": v(-436.48, 15.2) * mm});
            skLineSegment(sketch, "E342", {"start": v(-436.48, 15.2) * mm, "end": v(-453.85, 18.85) * mm});
            skLineSegment(sketch, "E343", {"start": v(-453.85, 18.85) * mm, "end": v(-478.4, -98.1) * mm});
            skLineSegment(sketch, "E344", {"start": v(-478.4, -98.1) * mm, "end": v(-461.02, -101.75) * mm});
            skArc(sketch, "E345", {"start": v(-461.02, -101.75) * mm, "mid": v(-458.48, -105.49) * mm, "end": v(-462.12, -108.18) * mm});
            skLineSegment(sketch, "E346", {"start": v(-462.12, -108.18) * mm, "end": v(-496.5, -272.07) * mm});
            skArc(sketch, "E347", {"start": v(-496.5, -272.07) * mm, "mid": v(-494.25, -276) * mm, "end": v(-498.1, -278.4) * mm});
            skLineSegment(sketch, "E348", {"start": v(-498.1, -278.4) * mm, "end": v(-515.46, -274.75) * mm});
            skLineSegment(sketch, "E349", {"start": v(-515.46, -274.75) * mm, "end": v(-540, -391.7) * mm});
            skLineSegment(sketch, "E350", {"start": v(-540, -391.7) * mm, "end": v(-522.63, -395.35) * mm});
            skArc(sketch, "E351", {"start": v(-522.63, -395.35) * mm, "mid": v(-520.1, -399.1) * mm, "end": v(-523.73, -401.78) * mm});
            skLineSegment(sketch, "E352", {"start": v(-523.73, -401.78) * mm, "end": v(-556.62, -558.55) * mm});
            skLineSegment(sketch, "E353", {"start": v(-556.62, -558.55) * mm, "end": v(-513.07, -567.69) * mm});
            skLineSegment(sketch, "E354", {"start": v(-513.07, -567.69) * mm, "end": v(-502.86, -519) * mm});
            skArc(sketch, "E355", {"start": v(-502.86, -519) * mm, "mid": v(-499.11, -516.45) * mm, "end": v(-496.42, -520.1) * mm});
            skLineSegment(sketch, "E356", {"start": v(-496.42, -520.1) * mm, "end": v(-449.97, -529.84) * mm});
            skArc(sketch, "E357", {"start": v(-449.97, -529.84) * mm, "mid": v(-446.05, -527.58) * mm, "end": v(-443.65, -531.42) * mm});
            skLineSegment(sketch, "E358", {"start": v(-443.65, -531.42) * mm, "end": v(-453.86, -580.11) * mm});
            skLineSegment(sketch, "E359", {"start": v(-453.86, -580.11) * mm, "end": v(-415.2, -588.22) * mm});
            skLineSegment(sketch, "E360", {"start": v(-415.2, -588.22) * mm, "end": v(-404.99, -539.53) * mm});
            skArc(sketch, "E361", {"start": v(-404.99, -539.53) * mm, "mid": v(-401.25, -536.99) * mm, "end": v(-398.55, -540.63) * mm});
            skLineSegment(sketch, "E362", {"start": v(-398.55, -540.63) * mm, "end": v(-352.1, -550.37) * mm});
            skArc(sketch, "E363", {"start": v(-352.1, -550.37) * mm, "mid": v(-348.18, -548.12) * mm, "end": v(-345.78, -551.96) * mm});
            skLineSegment(sketch, "E364", {"start": v(-345.78, -551.96) * mm, "end": v(-356, -600.65) * mm});
            skLineSegment(sketch, "E365", {"start": v(-356, -600.65) * mm, "end": v(-312.44, -609.79) * mm});
            skLineSegment(sketch, "E366", {"start": v(-312.44, -609.79) * mm, "end": v(-279.55, -453.02) * mm});
            skArc(sketch, "E367", {"start": v(-279.55, -453.02) * mm, "mid": v(-281.8, -449.1) * mm, "end": v(-277.96, -446.7) * mm});
            skLineSegment(sketch, "E368", {"start": v(-277.96, -446.7) * mm, "end": v(-260.6, -450.34) * mm});
            skLineSegment(sketch, "E369", {"start": v(-260.6, -450.34) * mm, "end": v(-236.05, -333.39) * mm});
            skLineSegment(sketch, "E370", {"start": v(-236.05, -333.39) * mm, "end": v(-253.42, -329.74) * mm});
            skArc(sketch, "E371", {"start": v(-253.42, -329.74) * mm, "mid": v(-255.96, -326) * mm, "end": v(-252.33, -323.3) * mm});
            skLineSegment(sketch, "E372", {"start": v(-252.33, -323.3) * mm, "end": v(-217.94, -159.42) * mm});
            skArc(sketch, "E373", {"start": v(-217.94, -159.42) * mm, "mid": v(-220.2, -155.49) * mm, "end": v(-216.35, -153.09) * mm});
            skLineSegment(sketch, "E374", {"start": v(-216.35, -153.09) * mm, "end": v(-198.98, -156.73) * mm});
            skLineSegment(sketch, "E375", {"start": v(-198.98, -156.73) * mm, "end": v(-174.44, -39.78) * mm});
            skLineSegment(sketch, "E376", {"start": v(-174.44, -39.78) * mm, "end": v(-191.81, -36.14) * mm});
            skArc(sketch, "E377", {"start": v(-191.81, -36.14) * mm, "mid": v(-194.35, -32.4) * mm, "end": v(-190.72, -29.7) * mm});
            skLineSegment(sketch, "E378", {"start": v(-190.72, -29.7) * mm, "end": v(-156.32, 134.19) * mm});
            skArc(sketch, "E379", {"start": v(-156.32, 134.19) * mm, "mid": v(-158.58, 138.12) * mm, "end": v(-154.74, 140.52) * mm});
            skLineSegment(sketch, "E380", {"start": v(-154.74, 140.52) * mm, "end": v(-137.37, 136.87) * mm});
            skLineSegment(sketch, "E381", {"start": v(-137.37, 136.87) * mm, "end": v(-112.83, 253.82) * mm});
            skLineSegment(sketch, "E382", {"start": v(-112.83, 253.82) * mm, "end": v(-130.2, 257.47) * mm});
            skArc(sketch, "E383", {"start": v(-130.2, 257.47) * mm, "mid": v(-132.74, 261.21) * mm, "end": v(-129.1, 263.9) * mm});
            skLineSegment(sketch, "E384", {"start": v(-129.1, 263.9) * mm, "end": v(-94.71, 427.8) * mm});
            skArc(sketch, "E385", {"start": v(-94.71, 427.8) * mm, "mid": v(-96.97, 431.72) * mm, "end": v(-93.13, 434.12) * mm});
            skLineSegment(sketch, "E386", {"start": v(-93.13, 434.12) * mm, "end": v(-75.76, 430.48) * mm});
            skLineSegment(sketch, "E387", {"start": v(-75.76, 430.48) * mm, "end": v(-51.22, 547.43) * mm});
            skLineSegment(sketch, "E388", {"start": v(-51.22, 547.43) * mm, "end": v(-68.59, 551.08) * mm});
            skArc(sketch, "E389", {"start": v(-68.59, 551.08) * mm, "mid": v(-71.13, 554.82) * mm, "end": v(-67.5, 557.5) * mm});
            skLineSegment(sketch, "E390", {"start": v(-67.5, 557.5) * mm, "end": v(-32.22, 725.61) * mm});
            skLineSegment(sketch, "E391", {"start": v(-32.22, 725.61) * mm, "end": v(131, 779.12) * mm});
            skArc(sketch, "E392", {"start": v(131, 779.12) * mm, "mid": v(133.28, 783.04) * mm, "end": v(137.28, 780.91) * mm});
            skLineSegment(sketch, "E393", {"start": v(137.28, 780.91) * mm, "end": v(142.8, 764.04) * mm});
            skLineSegment(sketch, "E394", {"start": v(142.8, 764.04) * mm, "end": v(256.36, 801.27) * mm});
            skLineSegment(sketch, "E395", {"start": v(256.36, 801.27) * mm, "end": v(250.83, 818.13) * mm});
            skArc(sketch, "E396", {"start": v(250.83, 818.13) * mm, "mid": v(252.8, 822.2) * mm, "end": v(256.95, 820.4) * mm});
            skLineSegment(sketch, "E397", {"start": v(256.95, 820.4) * mm, "end": v(416.08, 872.56) * mm});
            skArc(sketch, "E398", {"start": v(416.08, 872.56) * mm, "mid": v(418.35, 876.48) * mm, "end": v(422.35, 874.36) * mm});
            skLineSegment(sketch, "E399", {"start": v(-505.5, 623.58) * mm, "end": v(-578.4, 623.58) * mm});
            skLineSegment(sketch, "E400", {"start": v(-578.4, 623.58) * mm, "end": v(-578.4, 739.58) * mm});
            skLineSegment(sketch, "E401", {"start": v(-578.4, 739.58) * mm, "end": v(-429.6, 739.58) * mm});
            skLineSegment(sketch, "E402", {"start": v(-429.6, 739.58) * mm, "end": v(-429.6, 489.78) * mm});
            skLineSegment(sketch, "E403", {"start": v(-429.6, 489.78) * mm, "end": v(-578.4, 489.78) * mm});
            skLineSegment(sketch, "E404", {"start": v(-578.4, 489.78) * mm, "end": v(-578.4, 605.78) * mm});
            skLineSegment(sketch, "E405", {"start": v(-578.4, 605.78) * mm, "end": v(-505.5, 605.78) * mm});
            skArc(sketch, "E406", {"start": v(-505.5, 605.78) * mm, "mid": v(-503.32, 606.7) * mm, "end": v(-502.4, 608.88) * mm});
            skLineSegment(sketch, "E407", {"start": v(-502.4, 608.88) * mm, "end": v(-502.4, 620.48) * mm});
            skArc(sketch, "E408", {"start": v(-502.4, 620.48) * mm, "mid": v(-503.32, 622.67) * mm, "end": v(-505.5, 623.58) * mm});
            skLineSegment(sketch, "E409", {"start": v(78.57, -899.68) * mm, "end": v(5.67, -899.68) * mm});
            skLineSegment(sketch, "E410", {"start": v(5.67, -899.68) * mm, "end": v(5.67, -783.68) * mm});
            skLineSegment(sketch, "E411", {"start": v(5.67, -783.68) * mm, "end": v(154.47, -783.68) * mm});
            skLineSegment(sketch, "E412", {"start": v(154.47, -783.68) * mm, "end": v(154.47, -1033.48) * mm});
            skLineSegment(sketch, "E413", {"start": v(154.47, -1033.48) * mm, "end": v(5.67, -1033.48) * mm});
            skLineSegment(sketch, "E414", {"start": v(5.67, -1033.48) * mm, "end": v(5.67, -917.48) * mm});
            skLineSegment(sketch, "E415", {"start": v(5.67, -917.48) * mm, "end": v(78.57, -917.48) * mm});
            skArc(sketch, "E416", {"start": v(78.57, -917.48) * mm, "mid": v(80.76, -916.57) * mm, "end": v(81.67, -914.38) * mm});
            skLineSegment(sketch, "E417", {"start": v(81.67, -914.38) * mm, "end": v(81.67, -902.78) * mm});
            skArc(sketch, "E418", {"start": v(81.67, -902.78) * mm, "mid": v(80.76, -900.59) * mm, "end": v(78.57, -899.68) * mm});
            skLineSegment(sketch, "E419", {"start": v(315.4, 608.68) * mm, "end": v(332.2, 615.12) * mm});
            skLineSegment(sketch, "E420", {"start": v(332.2, 615.12) * mm, "end": v(317.89, 652.47) * mm});
            skLineSegment(sketch, "E421", {"start": v(317.89, 652.47) * mm, "end": v(301.08, 646.03) * mm});
            skLineSegment(sketch, "E422", {"start": v(301.08, 646.03) * mm, "end": v(315.4, 608.68) * mm});
            skLineSegment(sketch, "E423", {"start": v(98.75, 525.67) * mm, "end": v(115.56, 532.11) * mm});
            skLineSegment(sketch, "E424", {"start": v(115.56, 532.11) * mm, "end": v(101.25, 569.46) * mm});
            skLineSegment(sketch, "E425", {"start": v(101.25, 569.46) * mm, "end": v(84.44, 563.02) * mm});
            skLineSegment(sketch, "E426", {"start": v(84.44, 563.02) * mm, "end": v(98.75, 525.67) * mm});
            skLineSegment(sketch, "E427", {"start": v(422.73, 328.54) * mm, "end": v(439.54, 334.98) * mm});
            skLineSegment(sketch, "E428", {"start": v(439.54, 334.98) * mm, "end": v(425.23, 372.33) * mm});
            skLineSegment(sketch, "E429", {"start": v(425.23, 372.33) * mm, "end": v(408.42, 365.9) * mm});
            skLineSegment(sketch, "E430", {"start": v(408.42, 365.9) * mm, "end": v(422.73, 328.54) * mm});
            skLineSegment(sketch, "E431", {"start": v(206.1, 245.53) * mm, "end": v(222.9, 251.97) * mm});
            skLineSegment(sketch, "E432", {"start": v(222.9, 251.97) * mm, "end": v(208.59, 289.32) * mm});
            skLineSegment(sketch, "E433", {"start": v(208.59, 289.32) * mm, "end": v(191.78, 282.88) * mm});
            skLineSegment(sketch, "E434", {"start": v(191.78, 282.88) * mm, "end": v(206.1, 245.53) * mm});
            skLineSegment(sketch, "E435", {"start": v(530.07, 48.4) * mm, "end": v(546.88, 54.84) * mm});
            skLineSegment(sketch, "E436", {"start": v(546.88, 54.84) * mm, "end": v(532.57, 92.2) * mm});
            skLineSegment(sketch, "E437", {"start": v(532.57, 92.2) * mm, "end": v(515.76, 85.75) * mm});
            skLineSegment(sketch, "E438", {"start": v(515.76, 85.75) * mm, "end": v(530.07, 48.4) * mm});
            skLineSegment(sketch, "E439", {"start": v(490.78, -71.34) * mm, "end": v(504.77, -82.68) * mm});
            skLineSegment(sketch, "E440", {"start": v(504.77, -82.68) * mm, "end": v(529.96, -51.6) * mm});
            skLineSegment(sketch, "E441", {"start": v(529.96, -51.6) * mm, "end": v(515.98, -40.27) * mm});
            skLineSegment(sketch, "E442", {"start": v(515.98, -40.27) * mm, "end": v(490.78, -71.34) * mm});
            skLineSegment(sketch, "E443", {"start": v(301.85, -304.37) * mm, "end": v(315.83, -315.7) * mm});
            skLineSegment(sketch, "E444", {"start": v(315.83, -315.7) * mm, "end": v(341.02, -284.64) * mm});
            skLineSegment(sketch, "E445", {"start": v(341.02, -284.64) * mm, "end": v(327.04, -273.3) * mm});
            skLineSegment(sketch, "E446", {"start": v(327.04, -273.3) * mm, "end": v(301.85, -304.37) * mm});
            skLineSegment(sketch, "E447", {"start": v(135.62, -169.6) * mm, "end": v(160.81, -138.53) * mm});
            skLineSegment(sketch, "E448", {"start": v(160.81, -138.53) * mm, "end": v(146.83, -127.2) * mm});
            skLineSegment(sketch, "E449", {"start": v(146.83, -127.2) * mm, "end": v(121.64, -158.26) * mm});
            skLineSegment(sketch, "E450", {"start": v(121.64, -158.26) * mm, "end": v(135.62, -169.6) * mm});
            skLineSegment(sketch, "E451", {"start": v(-239.77, -972.4) * mm, "end": v(-264.97, -1003.46) * mm});
            skLineSegment(sketch, "E452", {"start": v(-264.97, -1003.46) * mm, "end": v(-250.98, -1014.8) * mm});
            skLineSegment(sketch, "E453", {"start": v(-250.98, -1014.8) * mm, "end": v(-225.8, -983.73) * mm});
            skLineSegment(sketch, "E454", {"start": v(-225.8, -983.73) * mm, "end": v(-239.77, -972.4) * mm});
            skLineSegment(sketch, "E455", {"start": v(-406, -837.61) * mm, "end": v(-419.98, -826.28) * mm});
            skLineSegment(sketch, "E456", {"start": v(-419.98, -826.28) * mm, "end": v(-445.18, -857.35) * mm});
            skLineSegment(sketch, "E457", {"start": v(-445.18, -857.35) * mm, "end": v(-431.2, -868.69) * mm});
            skLineSegment(sketch, "E458", {"start": v(-431.2, -868.69) * mm, "end": v(-406, -837.61) * mm});
            skLineSegment(sketch, "E459", {"start": v(112.9, -537.4) * mm, "end": v(126.9, -548.74) * mm});
            skLineSegment(sketch, "E460", {"start": v(126.9, -548.74) * mm, "end": v(152.08, -517.67) * mm});
            skLineSegment(sketch, "E461", {"start": v(152.08, -517.67) * mm, "end": v(138.1, -506.33) * mm});
            skLineSegment(sketch, "E462", {"start": v(138.1, -506.33) * mm, "end": v(112.9, -537.4) * mm});
            skLineSegment(sketch, "E463", {"start": v(-53.32, -402.63) * mm, "end": v(-28.13, -371.56) * mm});
            skLineSegment(sketch, "E464", {"start": v(-28.13, -371.56) * mm, "end": v(-42.1, -360.22) * mm});
            skLineSegment(sketch, "E465", {"start": v(-42.1, -360.22) * mm, "end": v(-67.3, -391.3) * mm});
            skLineSegment(sketch, "E466", {"start": v(-67.3, -391.3) * mm, "end": v(-53.32, -402.63) * mm});
            skLineSegment(sketch, "E467", {"start": v(-50.84, -739.36) * mm, "end": v(-76.03, -770.43) * mm});
            skLineSegment(sketch, "E468", {"start": v(-76.03, -770.43) * mm, "end": v(-62.05, -781.77) * mm});
            skLineSegment(sketch, "E469", {"start": v(-62.05, -781.77) * mm, "end": v(-36.86, -750.7) * mm});
            skLineSegment(sketch, "E470", {"start": v(-36.86, -750.7) * mm, "end": v(-50.84, -739.36) * mm});
            skLineSegment(sketch, "E471", {"start": v(-217.06, -604.59) * mm, "end": v(-231.05, -593.25) * mm});
            skLineSegment(sketch, "E472", {"start": v(-231.05, -593.25) * mm, "end": v(-256.24, -624.32) * mm});
            skLineSegment(sketch, "E473", {"start": v(-256.24, -624.32) * mm, "end": v(-242.26, -635.66) * mm});
            skLineSegment(sketch, "E474", {"start": v(-242.26, -635.66) * mm, "end": v(-217.06, -604.59) * mm});
            skLineSegment(sketch, "E475", {"start": v(-156.41, -667.92) * mm, "end": v(-167.75, -681.9) * mm});
            skLineSegment(sketch, "E476", {"start": v(-167.75, -681.9) * mm, "end": v(-136.68, -707.1) * mm});
            skLineSegment(sketch, "E477", {"start": v(-136.68, -707.1) * mm, "end": v(-125.34, -693.11) * mm});
            skLineSegment(sketch, "E478", {"start": v(-125.34, -693.11) * mm, "end": v(-156.41, -667.92) * mm});
            skLineSegment(sketch, "E479", {"start": v(387.86, 1107.2) * mm, "end": v(382.25, 1124.3) * mm});
            skLineSegment(sketch, "E480", {"start": v(382.25, 1124.3) * mm, "end": v(420.27, 1136.76) * mm});
            skLineSegment(sketch, "E481", {"start": v(420.27, 1136.76) * mm, "end": v(425.87, 1119.66) * mm});
            skLineSegment(sketch, "E482", {"start": v(425.87, 1119.66) * mm, "end": v(387.86, 1107.2) * mm});
            skLineSegment(sketch, "E483", {"start": v(460.13, 886.74) * mm, "end": v(454.52, 903.84) * mm});
            skLineSegment(sketch, "E484", {"start": v(454.52, 903.84) * mm, "end": v(492.53, 916.3) * mm});
            skLineSegment(sketch, "E485", {"start": v(492.53, 916.3) * mm, "end": v(498.14, 899.2) * mm});
            skLineSegment(sketch, "E486", {"start": v(498.14, 899.2) * mm, "end": v(460.13, 886.74) * mm});
            skLineSegment(sketch, "E487", {"start": v(102.79, 1013.75) * mm, "end": v(97.18, 1030.85) * mm});
            skLineSegment(sketch, "E488", {"start": v(97.18, 1030.85) * mm, "end": v(135.19, 1043.31) * mm});
            skLineSegment(sketch, "E489", {"start": v(135.19, 1043.31) * mm, "end": v(140.8, 1026.2) * mm});
            skLineSegment(sketch, "E490", {"start": v(140.8, 1026.2) * mm, "end": v(102.79, 1013.75) * mm});
            skLineSegment(sketch, "E491", {"start": v(175.05, 793.3) * mm, "end": v(169.44, 810.4) * mm});
            skLineSegment(sketch, "E492", {"start": v(169.44, 810.4) * mm, "end": v(207.45, 822.86) * mm});
            skLineSegment(sketch, "E493", {"start": v(207.45, 822.86) * mm, "end": v(213.06, 805.75) * mm});
            skLineSegment(sketch, "E494", {"start": v(213.06, 805.75) * mm, "end": v(175.05, 793.3) * mm});
            skLineSegment(sketch, "E495", {"start": v(-182.29, 920.3) * mm, "end": v(-187.9, 937.4) * mm});
            skLineSegment(sketch, "E496", {"start": v(-187.9, 937.4) * mm, "end": v(-149.89, 949.87) * mm});
            skLineSegment(sketch, "E497", {"start": v(-149.89, 949.87) * mm, "end": v(-144.28, 932.76) * mm});
            skLineSegment(sketch, "E498", {"start": v(-144.28, 932.76) * mm, "end": v(-182.29, 920.3) * mm});
            skLineSegment(sketch, "E499", {"start": v(-250.41, 814.28) * mm, "end": v(-268.03, 817.97) * mm});
            skLineSegment(sketch, "E500", {"start": v(-268.03, 817.97) * mm, "end": v(-259.81, 857.12) * mm});
            skLineSegment(sketch, "E501", {"start": v(-259.81, 857.12) * mm, "end": v(-242.2, 853.42) * mm});
            skLineSegment(sketch, "E502", {"start": v(-242.2, 853.42) * mm, "end": v(-250.41, 814.28) * mm});
            skLineSegment(sketch, "E503", {"start": v(-312.02, 520.67) * mm, "end": v(-329.64, 524.37) * mm});
            skLineSegment(sketch, "E504", {"start": v(-329.64, 524.37) * mm, "end": v(-321.42, 563.52) * mm});
            skLineSegment(sketch, "E505", {"start": v(-321.42, 563.52) * mm, "end": v(-303.8, 559.82) * mm});
            skLineSegment(sketch, "E506", {"start": v(-303.8, 559.82) * mm, "end": v(-312.02, 520.67) * mm});
            skLineSegment(sketch, "E507", {"start": v(-102.58, 476.72) * mm, "end": v(-94.37, 515.87) * mm});
            skLineSegment(sketch, "E508", {"start": v(-94.37, 515.87) * mm, "end": v(-76.75, 512.17) * mm});
            skLineSegment(sketch, "E509", {"start": v(-76.75, 512.17) * mm, "end": v(-84.97, 473.03) * mm});
            skLineSegment(sketch, "E510", {"start": v(-84.97, 473.03) * mm, "end": v(-102.58, 476.72) * mm});
            skLineSegment(sketch, "E511", {"start": v(-488.64, -321) * mm, "end": v(-496.85, -360.15) * mm});
            skLineSegment(sketch, "E512", {"start": v(-496.85, -360.15) * mm, "end": v(-514.47, -356.45) * mm});
            skLineSegment(sketch, "E513", {"start": v(-514.47, -356.45) * mm, "end": v(-506.26, -317.3) * mm});
            skLineSegment(sketch, "E514", {"start": v(-506.26, -317.3) * mm, "end": v(-488.64, -321) * mm});
            skLineSegment(sketch, "E515", {"start": v(-279.2, -364.95) * mm, "end": v(-261.58, -368.64) * mm});
            skLineSegment(sketch, "E516", {"start": v(-261.58, -368.64) * mm, "end": v(-269.8, -407.8) * mm});
            skLineSegment(sketch, "E517", {"start": v(-269.8, -407.8) * mm, "end": v(-287.42, -404.1) * mm});
            skLineSegment(sketch, "E518", {"start": v(-287.42, -404.1) * mm, "end": v(-279.2, -364.95) * mm});
            skLineSegment(sketch, "E519", {"start": v(-373.63, 227.07) * mm, "end": v(-391.25, 230.76) * mm});
            skLineSegment(sketch, "E520", {"start": v(-391.25, 230.76) * mm, "end": v(-383.03, 269.9) * mm});
            skLineSegment(sketch, "E521", {"start": v(-383.03, 269.9) * mm, "end": v(-365.42, 266.21) * mm});
            skLineSegment(sketch, "E522", {"start": v(-365.42, 266.21) * mm, "end": v(-373.63, 227.07) * mm});
            skLineSegment(sketch, "E523", {"start": v(-164.2, 183.12) * mm, "end": v(-155.98, 222.26) * mm});
            skLineSegment(sketch, "E524", {"start": v(-155.98, 222.26) * mm, "end": v(-138.36, 218.57) * mm});
            skLineSegment(sketch, "E525", {"start": v(-138.36, 218.57) * mm, "end": v(-146.58, 179.42) * mm});
            skLineSegment(sketch, "E526", {"start": v(-146.58, 179.42) * mm, "end": v(-164.2, 183.12) * mm});
            skLineSegment(sketch, "E527", {"start": v(-427.03, -27.4) * mm, "end": v(-435.24, -66.54) * mm});
            skLineSegment(sketch, "E528", {"start": v(-435.24, -66.54) * mm, "end": v(-452.86, -62.84) * mm});
            skLineSegment(sketch, "E529", {"start": v(-452.86, -62.84) * mm, "end": v(-444.65, -23.7) * mm});
            skLineSegment(sketch, "E530", {"start": v(-444.65, -23.7) * mm, "end": v(-427.03, -27.4) * mm});
            skLineSegment(sketch, "E531", {"start": v(-217.6, -71.34) * mm, "end": v(-199.97, -75.04) * mm});
            skLineSegment(sketch, "E532", {"start": v(-199.97, -75.04) * mm, "end": v(-208.19, -114.19) * mm});
            skLineSegment(sketch, "E533", {"start": v(-208.19, -114.19) * mm, "end": v(-225.8, -110.49) * mm});
            skLineSegment(sketch, "E534", {"start": v(-225.8, -110.49) * mm, "end": v(-217.6, -71.34) * mm});
            skLineSegment(sketch, "E535", {"start": v(-305, -64.24) * mm, "end": v(-308.7, -81.86) * mm});
            skLineSegment(sketch, "E536", {"start": v(-308.7, -81.86) * mm, "end": v(-347.84, -73.64) * mm});
            skLineSegment(sketch, "E537", {"start": v(-347.84, -73.64) * mm, "end": v(-344.14, -56.03) * mm});
            skLineSegment(sketch, "E538", {"start": v(-344.14, -56.03) * mm, "end": v(-305, -64.24) * mm});
            skLineSegment(sketch, "E539", {"start": v(375.62, 97.78) * mm, "end": v(415.12, 91.5) * mm});
            skLineSegment(sketch, "E540", {"start": v(415.12, 91.5) * mm, "end": v(411.22, 66.95) * mm});
            skLineSegment(sketch, "E541", {"start": v(396.25, 94.5) * mm, "end": v(392.62, 71.72) * mm});
            skLineSegment(sketch, "E542", {"start": v(362.09, 12.55) * mm, "end": v(398.04, -15.91) * mm});
            skLineSegment(sketch, "E543", {"start": v(354.71, -31.25) * mm, "end": v(354.76, -30.95) * mm});
            skLineSegment(sketch, "E544", {"start": v(354.76, -30.95) * mm, "end": v(354.81, -30.65) * mm});
            skLineSegment(sketch, "E545", {"start": v(354.81, -30.65) * mm, "end": v(354.87, -30.35) * mm});
            skLineSegment(sketch, "E546", {"start": v(354.87, -30.35) * mm, "end": v(354.94, -30.06) * mm});
            skLineSegment(sketch, "E547", {"start": v(354.94, -30.06) * mm, "end": v(355.01, -29.76) * mm});
            skLineSegment(sketch, "E548", {"start": v(355.01, -29.76) * mm, "end": v(355.1, -29.47) * mm});
            skLineSegment(sketch, "E549", {"start": v(355.1, -29.47) * mm, "end": v(355.19, -29.19) * mm});
            skLineSegment(sketch, "E550", {"start": v(355.19, -29.19) * mm, "end": v(355.28, -28.9) * mm});
            skLineSegment(sketch, "E551", {"start": v(355.28, -28.9) * mm, "end": v(355.5, -28.34) * mm});
            skLineSegment(sketch, "E552", {"start": v(355.5, -28.34) * mm, "end": v(355.74, -27.8) * mm});
            skLineSegment(sketch, "E553", {"start": v(355.74, -27.8) * mm, "end": v(356.01, -27.26) * mm});
            skLineSegment(sketch, "E554", {"start": v(356.01, -27.26) * mm, "end": v(356.3, -26.74) * mm});
            skLineSegment(sketch, "E555", {"start": v(356.3, -26.74) * mm, "end": v(356.63, -26.23) * mm});
            skLineSegment(sketch, "E556", {"start": v(356.63, -26.23) * mm, "end": v(356.97, -25.74) * mm});
            skLineSegment(sketch, "E557", {"start": v(356.97, -25.74) * mm, "end": v(357.34, -25.27) * mm});
            skLineSegment(sketch, "E558", {"start": v(357.34, -25.27) * mm, "end": v(357.54, -25.04) * mm});
            skLineSegment(sketch, "E559", {"start": v(357.54, -25.04) * mm, "end": v(357.74, -24.82) * mm});
            skLineSegment(sketch, "E560", {"start": v(357.74, -24.82) * mm, "end": v(357.94, -24.6) * mm});
            skLineSegment(sketch, "E561", {"start": v(357.94, -24.6) * mm, "end": v(358.15, -24.38) * mm});
            skLineSegment(sketch, "E562", {"start": v(358.15, -24.38) * mm, "end": v(358.37, -24.17) * mm});
            skLineSegment(sketch, "E563", {"start": v(358.37, -24.17) * mm, "end": v(358.6, -23.97) * mm});
            skLineSegment(sketch, "E564", {"start": v(358.6, -23.97) * mm, "end": v(358.82, -23.77) * mm});
            skLineSegment(sketch, "E565", {"start": v(358.82, -23.77) * mm, "end": v(359.05, -23.58) * mm});
            skLineSegment(sketch, "E566", {"start": v(359.05, -23.58) * mm, "end": v(359.3, -23.39) * mm});
            skLineSegment(sketch, "E567", {"start": v(359.3, -23.39) * mm, "end": v(359.53, -23.2) * mm});
            skLineSegment(sketch, "E568", {"start": v(359.53, -23.2) * mm, "end": v(359.88, -22.98) * mm});
            skLineSegment(sketch, "E569", {"start": v(359.88, -22.98) * mm, "end": v(360.23, -22.75) * mm});
            skLineSegment(sketch, "E570", {"start": v(360.23, -22.75) * mm, "end": v(360.59, -22.54) * mm});
            skLineSegment(sketch, "E571", {"start": v(360.59, -22.54) * mm, "end": v(360.95, -22.34) * mm});
            skLineSegment(sketch, "E572", {"start": v(360.95, -22.34) * mm, "end": v(361.31, -22.14) * mm});
            skLineSegment(sketch, "E573", {"start": v(361.31, -22.14) * mm, "end": v(361.68, -21.96) * mm});
            skLineSegment(sketch, "E574", {"start": v(361.68, -21.96) * mm, "end": v(362.05, -21.78) * mm});
            skLineSegment(sketch, "E575", {"start": v(362.05, -21.78) * mm, "end": v(362.43, -21.62) * mm});
            skLineSegment(sketch, "E576", {"start": v(362.43, -21.62) * mm, "end": v(362.8, -21.46) * mm});
            skLineSegment(sketch, "E577", {"start": v(362.8, -21.46) * mm, "end": v(363.2, -21.32) * mm});
            skLineSegment(sketch, "E578", {"start": v(363.2, -21.32) * mm, "end": v(363.58, -21.18) * mm});
            skLineSegment(sketch, "E579", {"start": v(363.58, -21.18) * mm, "end": v(363.97, -21.06) * mm});
            skLineSegment(sketch, "E580", {"start": v(363.97, -21.06) * mm, "end": v(364.36, -20.94) * mm});
            skLineSegment(sketch, "E581", {"start": v(364.36, -20.94) * mm, "end": v(364.76, -20.84) * mm});
            skLineSegment(sketch, "E582", {"start": v(364.76, -20.84) * mm, "end": v(365.16, -20.74) * mm});
            skLineSegment(sketch, "E583", {"start": v(365.16, -20.74) * mm, "end": v(365.56, -20.66) * mm});
            skLineSegment(sketch, "E584", {"start": v(365.56, -20.66) * mm, "end": v(365.96, -20.58) * mm});
            skLineSegment(sketch, "E585", {"start": v(365.96, -20.58) * mm, "end": v(366.37, -20.52) * mm});
            skLineSegment(sketch, "E586", {"start": v(366.37, -20.52) * mm, "end": v(366.77, -20.47) * mm});
            skLineSegment(sketch, "E587", {"start": v(366.77, -20.47) * mm, "end": v(367.18, -20.42) * mm});
            skLineSegment(sketch, "E588", {"start": v(367.18, -20.42) * mm, "end": v(367.59, -20.39) * mm});
            skLineSegment(sketch, "E589", {"start": v(367.59, -20.39) * mm, "end": v(368, -20.36) * mm});
            skLineSegment(sketch, "E590", {"start": v(368, -20.36) * mm, "end": v(368.4, -20.35) * mm});
            skLineSegment(sketch, "E591", {"start": v(368.4, -20.35) * mm, "end": v(368.82, -20.35) * mm});
            skLineSegment(sketch, "E592", {"start": v(368.82, -20.35) * mm, "end": v(369.23, -20.36) * mm});
            skLineSegment(sketch, "E593", {"start": v(369.23, -20.36) * mm, "end": v(369.64, -20.37) * mm});
            skLineSegment(sketch, "E594", {"start": v(369.64, -20.37) * mm, "end": v(370.05, -20.4) * mm});
            skLineSegment(sketch, "E595", {"start": v(370.05, -20.4) * mm, "end": v(370.46, -20.44) * mm});
            skLineSegment(sketch, "E596", {"start": v(370.46, -20.44) * mm, "end": v(370.87, -20.5) * mm});
            skLineSegment(sketch, "E597", {"start": v(370.87, -20.5) * mm, "end": v(371.28, -20.55) * mm});
            skLineSegment(sketch, "E598", {"start": v(371.28, -20.55) * mm, "end": v(371.7, -20.63) * mm});
            skLineSegment(sketch, "E599", {"start": v(371.7, -20.63) * mm, "end": v(372.1, -20.7) * mm});
            skLineSegment(sketch, "E600", {"start": v(372.1, -20.7) * mm, "end": v(372.53, -20.77) * mm});
            skLineSegment(sketch, "E601", {"start": v(372.53, -20.77) * mm, "end": v(372.96, -20.84) * mm});
            skLineSegment(sketch, "E602", {"start": v(372.96, -20.84) * mm, "end": v(373.38, -20.92) * mm});
            skLineSegment(sketch, "E603", {"start": v(373.38, -20.92) * mm, "end": v(373.8, -21.02) * mm});
            skLineSegment(sketch, "E604", {"start": v(373.8, -21.02) * mm, "end": v(374.22, -21.12) * mm});
            skLineSegment(sketch, "E605", {"start": v(374.22, -21.12) * mm, "end": v(374.63, -21.23) * mm});
            skLineSegment(sketch, "E606", {"start": v(374.63, -21.23) * mm, "end": v(375.04, -21.36) * mm});
            skLineSegment(sketch, "E607", {"start": v(375.04, -21.36) * mm, "end": v(375.45, -21.5) * mm});
            skLineSegment(sketch, "E608", {"start": v(375.45, -21.5) * mm, "end": v(375.85, -21.64) * mm});
            skLineSegment(sketch, "E609", {"start": v(375.85, -21.64) * mm, "end": v(376.25, -21.79) * mm});
            skLineSegment(sketch, "E610", {"start": v(376.25, -21.79) * mm, "end": v(376.65, -21.95) * mm});
            skLineSegment(sketch, "E611", {"start": v(376.65, -21.95) * mm, "end": v(377.04, -22.13) * mm});
            skLineSegment(sketch, "E612", {"start": v(377.04, -22.13) * mm, "end": v(377.42, -22.3) * mm});
            skLineSegment(sketch, "E613", {"start": v(377.42, -22.3) * mm, "end": v(377.8, -22.5) * mm});
            skLineSegment(sketch, "E614", {"start": v(377.8, -22.5) * mm, "end": v(378.18, -22.7) * mm});
            skLineSegment(sketch, "E615", {"start": v(378.18, -22.7) * mm, "end": v(378.55, -22.92) * mm});
            skLineSegment(sketch, "E616", {"start": v(378.55, -22.92) * mm, "end": v(378.91, -23.14) * mm});
            skLineSegment(sketch, "E617", {"start": v(378.91, -23.14) * mm, "end": v(379.27, -23.37) * mm});
            skLineSegment(sketch, "E618", {"start": v(379.27, -23.37) * mm, "end": v(379.63, -23.6) * mm});
            skLineSegment(sketch, "E619", {"start": v(379.63, -23.6) * mm, "end": v(379.97, -23.85) * mm});
            skLineSegment(sketch, "E620", {"start": v(379.97, -23.85) * mm, "end": v(380.32, -24.1) * mm});
            skLineSegment(sketch, "E621", {"start": v(380.32, -24.1) * mm, "end": v(380.65, -24.37) * mm});
            skLineSegment(sketch, "E622", {"start": v(380.65, -24.37) * mm, "end": v(380.98, -24.65) * mm});
            skLineSegment(sketch, "E623", {"start": v(380.98, -24.65) * mm, "end": v(381.3, -24.93) * mm});
            skLineSegment(sketch, "E624", {"start": v(381.3, -24.93) * mm, "end": v(381.62, -25.22) * mm});
            skLineSegment(sketch, "E625", {"start": v(381.62, -25.22) * mm, "end": v(381.93, -25.51) * mm});
            skLineSegment(sketch, "E626", {"start": v(381.93, -25.51) * mm, "end": v(382.23, -25.82) * mm});
            skLineSegment(sketch, "E627", {"start": v(382.23, -25.82) * mm, "end": v(382.52, -26.13) * mm});
            skLineSegment(sketch, "E628", {"start": v(382.52, -26.13) * mm, "end": v(382.8, -26.46) * mm});
            skLineSegment(sketch, "E629", {"start": v(382.8, -26.46) * mm, "end": v(383.09, -26.79) * mm});
            skLineSegment(sketch, "E630", {"start": v(383.09, -26.79) * mm, "end": v(383.36, -27.12) * mm});
            skLineSegment(sketch, "E631", {"start": v(383.36, -27.12) * mm, "end": v(383.62, -27.47) * mm});
            skLineSegment(sketch, "E632", {"start": v(383.62, -27.47) * mm, "end": v(383.9, -27.89) * mm});
            skLineSegment(sketch, "E633", {"start": v(383.9, -27.89) * mm, "end": v(384.18, -28.32) * mm});
            skLineSegment(sketch, "E634", {"start": v(384.18, -28.32) * mm, "end": v(384.42, -28.77) * mm});
            skLineSegment(sketch, "E635", {"start": v(384.42, -28.77) * mm, "end": v(384.64, -29.22) * mm});
            skLineSegment(sketch, "E636", {"start": v(384.64, -29.22) * mm, "end": v(384.84, -29.69) * mm});
            skLineSegment(sketch, "E637", {"start": v(384.84, -29.69) * mm, "end": v(385, -30.16) * mm});
            skLineSegment(sketch, "E638", {"start": v(385, -30.16) * mm, "end": v(385.16, -30.65) * mm});
            skLineSegment(sketch, "E639", {"start": v(385.16, -30.65) * mm, "end": v(385.28, -31.13) * mm});
            skLineSegment(sketch, "E640", {"start": v(385.28, -31.13) * mm, "end": v(385.38, -31.63) * mm});
            skLineSegment(sketch, "E641", {"start": v(385.38, -31.63) * mm, "end": v(385.45, -32.13) * mm});
            skLineSegment(sketch, "E642", {"start": v(385.45, -32.13) * mm, "end": v(385.5, -32.63) * mm});
            skLineSegment(sketch, "E643", {"start": v(385.5, -32.63) * mm, "end": v(385.53, -33.13) * mm});
            skLineSegment(sketch, "E644", {"start": v(385.53, -33.13) * mm, "end": v(385.53, -33.64) * mm});
            skLineSegment(sketch, "E645", {"start": v(385.53, -33.64) * mm, "end": v(385.5, -34.15) * mm});
            skLineSegment(sketch, "E646", {"start": v(385.5, -34.15) * mm, "end": v(385.45, -34.65) * mm});
            skLineSegment(sketch, "E647", {"start": v(385.45, -34.65) * mm, "end": v(385.37, -35.16) * mm});
            skLineSegment(sketch, "E648", {"start": v(385.37, -35.16) * mm, "end": v(385.31, -35.45) * mm});
            skLineSegment(sketch, "E649", {"start": v(385.31, -35.45) * mm, "end": v(385.25, -35.74) * mm});
            skLineSegment(sketch, "E650", {"start": v(385.25, -35.74) * mm, "end": v(385.1, -36.32) * mm});
            skLineSegment(sketch, "E651", {"start": v(385.1, -36.32) * mm, "end": v(384.93, -36.88) * mm});
            skLineSegment(sketch, "E652", {"start": v(384.93, -36.88) * mm, "end": v(384.72, -37.44) * mm});
            skLineSegment(sketch, "E653", {"start": v(384.72, -37.44) * mm, "end": v(384.5, -37.98) * mm});
            skLineSegment(sketch, "E654", {"start": v(384.5, -37.98) * mm, "end": v(384.24, -38.51) * mm});
            skLineSegment(sketch, "E655", {"start": v(384.24, -38.51) * mm, "end": v(383.96, -39.03) * mm});
            skLineSegment(sketch, "E656", {"start": v(383.96, -39.03) * mm, "end": v(383.65, -39.53) * mm});
            skLineSegment(sketch, "E657", {"start": v(383.65, -39.53) * mm, "end": v(383.32, -40.02) * mm});
            skLineSegment(sketch, "E658", {"start": v(383.32, -40.02) * mm, "end": v(382.96, -40.49) * mm});
            skLineSegment(sketch, "E659", {"start": v(382.96, -40.49) * mm, "end": v(382.58, -40.94) * mm});
            skLineSegment(sketch, "E660", {"start": v(382.58, -40.94) * mm, "end": v(382.18, -41.37) * mm});
            skLineSegment(sketch, "E661", {"start": v(382.18, -41.37) * mm, "end": v(381.76, -41.79) * mm});
            skLineSegment(sketch, "E662", {"start": v(381.76, -41.79) * mm, "end": v(381.31, -42.18) * mm});
            skLineSegment(sketch, "E663", {"start": v(381.31, -42.18) * mm, "end": v(381.08, -42.37) * mm});
            skLineSegment(sketch, "E664", {"start": v(381.08, -42.37) * mm, "end": v(380.85, -42.55) * mm});
            skLineSegment(sketch, "E665", {"start": v(380.85, -42.55) * mm, "end": v(380.6, -42.73) * mm});
            skLineSegment(sketch, "E666", {"start": v(380.6, -42.73) * mm, "end": v(380.36, -42.9) * mm});
            skLineSegment(sketch, "E667", {"start": v(380.36, -42.9) * mm, "end": v(380.03, -43.13) * mm});
            skLineSegment(sketch, "E668", {"start": v(380.03, -43.13) * mm, "end": v(379.7, -43.34) * mm});
            skLineSegment(sketch, "E669", {"start": v(379.7, -43.34) * mm, "end": v(379.35, -43.55) * mm});
            skLineSegment(sketch, "E670", {"start": v(379.35, -43.55) * mm, "end": v(379, -43.75) * mm});
            skLineSegment(sketch, "E671", {"start": v(379, -43.75) * mm, "end": v(378.65, -43.94) * mm});
            skLineSegment(sketch, "E672", {"start": v(378.65, -43.94) * mm, "end": v(378.29, -44.12) * mm});
            skLineSegment(sketch, "E673", {"start": v(378.29, -44.12) * mm, "end": v(377.93, -44.29) * mm});
            skLineSegment(sketch, "E674", {"start": v(377.93, -44.29) * mm, "end": v(377.56, -44.45) * mm});
            skLineSegment(sketch, "E675", {"start": v(377.56, -44.45) * mm, "end": v(377.2, -44.6) * mm});
            skLineSegment(sketch, "E676", {"start": v(377.2, -44.6) * mm, "end": v(376.82, -44.74) * mm});
            skLineSegment(sketch, "E677", {"start": v(376.82, -44.74) * mm, "end": v(376.45, -44.87) * mm});
            skLineSegment(sketch, "E678", {"start": v(376.45, -44.87) * mm, "end": v(376.07, -45) * mm});
            skLineSegment(sketch, "E679", {"start": v(376.07, -45) * mm, "end": v(375.69, -45.1) * mm});
            skLineSegment(sketch, "E680", {"start": v(375.69, -45.1) * mm, "end": v(375.3, -45.2) * mm});
            skLineSegment(sketch, "E681", {"start": v(375.3, -45.2) * mm, "end": v(374.92, -45.3) * mm});
            skLineSegment(sketch, "E682", {"start": v(374.92, -45.3) * mm, "end": v(374.53, -45.38) * mm});
            skLineSegment(sketch, "E683", {"start": v(374.53, -45.38) * mm, "end": v(374.14, -45.46) * mm});
            skLineSegment(sketch, "E684", {"start": v(374.14, -45.46) * mm, "end": v(373.75, -45.52) * mm});
            skLineSegment(sketch, "E685", {"start": v(373.75, -45.52) * mm, "end": v(373.35, -45.57) * mm});
            skLineSegment(sketch, "E686", {"start": v(373.35, -45.57) * mm, "end": v(372.96, -45.61) * mm});
            skLineSegment(sketch, "E687", {"start": v(372.96, -45.61) * mm, "end": v(372.56, -45.65) * mm});
            skLineSegment(sketch, "E688", {"start": v(372.56, -45.65) * mm, "end": v(372.16, -45.67) * mm});
            skLineSegment(sketch, "E689", {"start": v(372.16, -45.67) * mm, "end": v(371.77, -45.68) * mm});
            skLineSegment(sketch, "E690", {"start": v(371.77, -45.68) * mm, "end": v(371.37, -45.68) * mm});
            skLineSegment(sketch, "E691", {"start": v(371.37, -45.68) * mm, "end": v(370.97, -45.67) * mm});
            skLineSegment(sketch, "E692", {"start": v(370.97, -45.67) * mm, "end": v(370.57, -45.66) * mm});
            skLineSegment(sketch, "E693", {"start": v(370.57, -45.66) * mm, "end": v(370.17, -45.63) * mm});
            skLineSegment(sketch, "E694", {"start": v(370.17, -45.63) * mm, "end": v(369.77, -45.59) * mm});
            skLineSegment(sketch, "E695", {"start": v(369.77, -45.59) * mm, "end": v(369.38, -45.54) * mm});
            skLineSegment(sketch, "E696", {"start": v(369.38, -45.54) * mm, "end": v(368.98, -45.48) * mm});
            skLineSegment(sketch, "E697", {"start": v(368.98, -45.48) * mm, "end": v(368.58, -45.4) * mm});
            skLineSegment(sketch, "E698", {"start": v(368.58, -45.4) * mm, "end": v(368.19, -45.33) * mm});
            skLineSegment(sketch, "E699", {"start": v(368.19, -45.33) * mm, "end": v(367.78, -45.28) * mm});
            skLineSegment(sketch, "E700", {"start": v(367.78, -45.28) * mm, "end": v(367.38, -45.23) * mm});
            skLineSegment(sketch, "E701", {"start": v(367.38, -45.23) * mm, "end": v(366.98, -45.16) * mm});
            skLineSegment(sketch, "E702", {"start": v(366.98, -45.16) * mm, "end": v(366.58, -45.09) * mm});
            skLineSegment(sketch, "E703", {"start": v(366.58, -45.09) * mm, "end": v(366.18, -45) * mm});
            skLineSegment(sketch, "E704", {"start": v(366.18, -45) * mm, "end": v(365.79, -44.9) * mm});
            skLineSegment(sketch, "E705", {"start": v(365.79, -44.9) * mm, "end": v(365.4, -44.8) * mm});
            skLineSegment(sketch, "E706", {"start": v(365.4, -44.8) * mm, "end": v(365.01, -44.69) * mm});
            skLineSegment(sketch, "E707", {"start": v(365.01, -44.69) * mm, "end": v(364.63, -44.56) * mm});
            skLineSegment(sketch, "E708", {"start": v(364.63, -44.56) * mm, "end": v(364.25, -44.43) * mm});
            skLineSegment(sketch, "E709", {"start": v(364.25, -44.43) * mm, "end": v(363.87, -44.29) * mm});
            skLineSegment(sketch, "E710", {"start": v(363.87, -44.29) * mm, "end": v(363.5, -44.14) * mm});
            skLineSegment(sketch, "E711", {"start": v(363.5, -44.14) * mm, "end": v(363.13, -43.97) * mm});
            skLineSegment(sketch, "E712", {"start": v(363.13, -43.97) * mm, "end": v(362.77, -43.8) * mm});
            skLineSegment(sketch, "E713", {"start": v(362.77, -43.8) * mm, "end": v(362.4, -43.63) * mm});
            skLineSegment(sketch, "E714", {"start": v(362.4, -43.63) * mm, "end": v(362.05, -43.44) * mm});
            skLineSegment(sketch, "E715", {"start": v(362.05, -43.44) * mm, "end": v(361.7, -43.24) * mm});
            skLineSegment(sketch, "E716", {"start": v(361.7, -43.24) * mm, "end": v(361.35, -43.04) * mm});
            skLineSegment(sketch, "E717", {"start": v(361.35, -43.04) * mm, "end": v(361.01, -42.82) * mm});
            skLineSegment(sketch, "E718", {"start": v(361.01, -42.82) * mm, "end": v(360.68, -42.6) * mm});
            skLineSegment(sketch, "E719", {"start": v(360.68, -42.6) * mm, "end": v(360.35, -42.37) * mm});
            skLineSegment(sketch, "E720", {"start": v(360.35, -42.37) * mm, "end": v(360.02, -42.13) * mm});
            skLineSegment(sketch, "E721", {"start": v(360.02, -42.13) * mm, "end": v(359.7, -41.88) * mm});
            skLineSegment(sketch, "E722", {"start": v(359.7, -41.88) * mm, "end": v(359.4, -41.63) * mm});
            skLineSegment(sketch, "E723", {"start": v(359.4, -41.63) * mm, "end": v(359.09, -41.36) * mm});
            skLineSegment(sketch, "E724", {"start": v(359.09, -41.36) * mm, "end": v(358.79, -41.1) * mm});
            skLineSegment(sketch, "E725", {"start": v(358.79, -41.1) * mm, "end": v(358.5, -40.81) * mm});
            skLineSegment(sketch, "E726", {"start": v(358.5, -40.81) * mm, "end": v(358.21, -40.53) * mm});
            skLineSegment(sketch, "E727", {"start": v(358.21, -40.53) * mm, "end": v(357.93, -40.23) * mm});
            skLineSegment(sketch, "E728", {"start": v(357.93, -40.23) * mm, "end": v(357.66, -39.93) * mm});
            skLineSegment(sketch, "E729", {"start": v(357.66, -39.93) * mm, "end": v(357.4, -39.62) * mm});
            skLineSegment(sketch, "E730", {"start": v(357.4, -39.62) * mm, "end": v(357.14, -39.3) * mm});
            skLineSegment(sketch, "E731", {"start": v(357.14, -39.3) * mm, "end": v(356.8, -38.87) * mm});
            skLineSegment(sketch, "E732", {"start": v(356.8, -38.87) * mm, "end": v(356.5, -38.43) * mm});
            skLineSegment(sketch, "E733", {"start": v(356.5, -38.43) * mm, "end": v(356.2, -37.97) * mm});
            skLineSegment(sketch, "E734", {"start": v(356.2, -37.97) * mm, "end": v(355.94, -37.5) * mm});
            skLineSegment(sketch, "E735", {"start": v(355.94, -37.5) * mm, "end": v(355.7, -37.02) * mm});
            skLineSegment(sketch, "E736", {"start": v(355.7, -37.02) * mm, "end": v(355.48, -36.53) * mm});
            skLineSegment(sketch, "E737", {"start": v(355.48, -36.53) * mm, "end": v(355.29, -36.03) * mm});
            skLineSegment(sketch, "E738", {"start": v(355.29, -36.03) * mm, "end": v(355.12, -35.52) * mm});
            skLineSegment(sketch, "E739", {"start": v(355.12, -35.52) * mm, "end": v(354.98, -35) * mm});
            skLineSegment(sketch, "E740", {"start": v(354.98, -35) * mm, "end": v(354.86, -34.47) * mm});
            skLineSegment(sketch, "E741", {"start": v(354.86, -34.47) * mm, "end": v(354.77, -33.94) * mm});
            skLineSegment(sketch, "E742", {"start": v(354.77, -33.94) * mm, "end": v(354.7, -33.4) * mm});
            skLineSegment(sketch, "E743", {"start": v(354.7, -33.4) * mm, "end": v(354.67, -32.87) * mm});
            skLineSegment(sketch, "E744", {"start": v(354.67, -32.87) * mm, "end": v(354.65, -32.33) * mm});
            skLineSegment(sketch, "E745", {"start": v(354.65, -32.33) * mm, "end": v(354.67, -31.79) * mm});
            skLineSegment(sketch, "E746", {"start": v(354.67, -31.79) * mm, "end": v(354.71, -31.25) * mm});
            skLineSegment(sketch, "E747", {"start": v(357.18, -18.34) * mm, "end": v(396.46, -24.58) * mm});
            skLineSegment(sketch, "E748", {"start": v(-137.63, 722.08) * mm, "end": v(-167.42, 748.76) * mm});
            skLineSegment(sketch, "E749", {"start": v(-167.42, 748.76) * mm, "end": v(-150.83, 767.28) * mm});
            skLineSegment(sketch, "E750", {"start": v(-153.19, 736) * mm, "end": v(-137.8, 753.2) * mm});
            skLineSegment(sketch, "E751", {"start": v(-80.07, 786.37) * mm, "end": v(-94.85, 829.78) * mm});
            skLineSegment(sketch, "E752", {"start": v(-59.2, 809.66) * mm, "end": v(-88.98, 836.33) * mm});
            skLineSegment(sketch, "E753", {"start": v(-88.98, 836.33) * mm, "end": v(-77.1, 849.59) * mm});
            skLineSegment(sketch, "E754", {"start": v(-77.1, 849.59) * mm, "end": v(-76.8, 849.89) * mm});
            skLineSegment(sketch, "E755", {"start": v(-76.8, 849.89) * mm, "end": v(-76.5, 850.17) * mm});
            skLineSegment(sketch, "E756", {"start": v(-76.5, 850.17) * mm, "end": v(-76.18, 850.43) * mm});
            skLineSegment(sketch, "E757", {"start": v(-76.18, 850.43) * mm, "end": v(-75.85, 850.68) * mm});
            skLineSegment(sketch, "E758", {"start": v(-75.85, 850.68) * mm, "end": v(-75.51, 850.91) * mm});
            skLineSegment(sketch, "E759", {"start": v(-75.51, 850.91) * mm, "end": v(-75.16, 851.12) * mm});
            skLineSegment(sketch, "E760", {"start": v(-75.16, 851.12) * mm, "end": v(-74.8, 851.32) * mm});
            skLineSegment(sketch, "E761", {"start": v(-74.8, 851.32) * mm, "end": v(-74.43, 851.5) * mm});
            skLineSegment(sketch, "E762", {"start": v(-74.43, 851.5) * mm, "end": v(-74.05, 851.65) * mm});
            skLineSegment(sketch, "E763", {"start": v(-74.05, 851.65) * mm, "end": v(-73.66, 851.8) * mm});
            skLineSegment(sketch, "E764", {"start": v(-73.66, 851.8) * mm, "end": v(-73.27, 851.91) * mm});
            skLineSegment(sketch, "E765", {"start": v(-73.27, 851.91) * mm, "end": v(-72.87, 852.01) * mm});
            skLineSegment(sketch, "E766", {"start": v(-72.87, 852.01) * mm, "end": v(-72.47, 852.1) * mm});
            skLineSegment(sketch, "E767", {"start": v(-72.47, 852.1) * mm, "end": v(-72.06, 852.15) * mm});
            skLineSegment(sketch, "E768", {"start": v(-72.06, 852.15) * mm, "end": v(-71.65, 852.2) * mm});
            skLineSegment(sketch, "E769", {"start": v(-71.65, 852.2) * mm, "end": v(-71.23, 852.2) * mm});
            skLineSegment(sketch, "E770", {"start": v(-71.23, 852.2) * mm, "end": v(-70.76, 852.23) * mm});
            skLineSegment(sketch, "E771", {"start": v(-70.76, 852.23) * mm, "end": v(-70.3, 852.23) * mm});
            skLineSegment(sketch, "E772", {"start": v(-70.3, 852.23) * mm, "end": v(-69.83, 852.21) * mm});
            skLineSegment(sketch, "E773", {"start": v(-69.83, 852.21) * mm, "end": v(-69.37, 852.16) * mm});
            skLineSegment(sketch, "E774", {"start": v(-69.37, 852.16) * mm, "end": v(-68.9, 852.1) * mm});
            skLineSegment(sketch, "E775", {"start": v(-68.9, 852.1) * mm, "end": v(-68.46, 852) * mm});
            skLineSegment(sketch, "E776", {"start": v(-68.46, 852) * mm, "end": v(-68, 851.89) * mm});
            skLineSegment(sketch, "E777", {"start": v(-68, 851.89) * mm, "end": v(-67.57, 851.75) * mm});
            skLineSegment(sketch, "E778", {"start": v(-67.57, 851.75) * mm, "end": v(-67.13, 851.6) * mm});
            skLineSegment(sketch, "E779", {"start": v(-67.13, 851.6) * mm, "end": v(-66.7, 851.41) * mm});
            skLineSegment(sketch, "E780", {"start": v(-66.7, 851.41) * mm, "end": v(-66.29, 851.21) * mm});
            skLineSegment(sketch, "E781", {"start": v(-66.29, 851.21) * mm, "end": v(-65.88, 850.99) * mm});
            skLineSegment(sketch, "E782", {"start": v(-65.88, 850.99) * mm, "end": v(-65.49, 850.75) * mm});
            skLineSegment(sketch, "E783", {"start": v(-65.49, 850.75) * mm, "end": v(-65.1, 850.48) * mm});
            skLineSegment(sketch, "E784", {"start": v(-65.1, 850.48) * mm, "end": v(-64.73, 850.2) * mm});
            skLineSegment(sketch, "E785", {"start": v(-64.73, 850.2) * mm, "end": v(-64.37, 849.9) * mm});
            skLineSegment(sketch, "E786", {"start": v(-64.37, 849.9) * mm, "end": v(-64.02, 849.59) * mm});
            skLineSegment(sketch, "E787", {"start": v(-64.02, 849.59) * mm, "end": v(-63.68, 849.26) * mm});
            skLineSegment(sketch, "E788", {"start": v(-63.68, 849.26) * mm, "end": v(-63.36, 848.92) * mm});
            skLineSegment(sketch, "E789", {"start": v(-63.36, 848.92) * mm, "end": v(-63.06, 848.56) * mm});
            skLineSegment(sketch, "E790", {"start": v(-63.06, 848.56) * mm, "end": v(-62.78, 848.19) * mm});
            skLineSegment(sketch, "E791", {"start": v(-62.78, 848.19) * mm, "end": v(-62.52, 847.8) * mm});
            skLineSegment(sketch, "E792", {"start": v(-62.52, 847.8) * mm, "end": v(-62.28, 847.4) * mm});
            skLineSegment(sketch, "E793", {"start": v(-62.28, 847.4) * mm, "end": v(-62.07, 847) * mm});
            skLineSegment(sketch, "E794", {"start": v(-62.07, 847) * mm, "end": v(-61.87, 846.57) * mm});
            skLineSegment(sketch, "E795", {"start": v(-61.87, 846.57) * mm, "end": v(-61.7, 846.14) * mm});
            skLineSegment(sketch, "E796", {"start": v(-61.7, 846.14) * mm, "end": v(-61.54, 845.7) * mm});
            skLineSegment(sketch, "E797", {"start": v(-61.54, 845.7) * mm, "end": v(-61.4, 845.26) * mm});
            skLineSegment(sketch, "E798", {"start": v(-61.4, 845.26) * mm, "end": v(-61.3, 844.8) * mm});
            skLineSegment(sketch, "E799", {"start": v(-61.3, 844.8) * mm, "end": v(-61.2, 844.35) * mm});
            skLineSegment(sketch, "E800", {"start": v(-61.2, 844.35) * mm, "end": v(-61.15, 843.88) * mm});
            skLineSegment(sketch, "E801", {"start": v(-61.15, 843.88) * mm, "end": v(-61.1, 843.41) * mm});
            skLineSegment(sketch, "E802", {"start": v(-61.1, 843.41) * mm, "end": v(-61.07, 842.95) * mm});
            skLineSegment(sketch, "E803", {"start": v(-61.07, 842.95) * mm, "end": v(-61.05, 842.5) * mm});
            skLineSegment(sketch, "E804", {"start": v(-61.05, 842.5) * mm, "end": v(-61.06, 842.04) * mm});
            skLineSegment(sketch, "E805", {"start": v(-61.06, 842.04) * mm, "end": v(-61.09, 841.58) * mm});
            skLineSegment(sketch, "E806", {"start": v(-61.09, 841.58) * mm, "end": v(-61.14, 841.13) * mm});
            skLineSegment(sketch, "E807", {"start": v(-61.14, 841.13) * mm, "end": v(-61.22, 840.69) * mm});
            skLineSegment(sketch, "E808", {"start": v(-61.22, 840.69) * mm, "end": v(-61.32, 840.24) * mm});
            skLineSegment(sketch, "E809", {"start": v(-61.32, 840.24) * mm, "end": v(-61.44, 839.8) * mm});
            skLineSegment(sketch, "E810", {"start": v(-61.44, 839.8) * mm, "end": v(-61.58, 839.38) * mm});
            skLineSegment(sketch, "E811", {"start": v(-61.58, 839.38) * mm, "end": v(-61.74, 838.95) * mm});
            skLineSegment(sketch, "E812", {"start": v(-61.74, 838.95) * mm, "end": v(-61.93, 838.54) * mm});
            skLineSegment(sketch, "E813", {"start": v(-61.93, 838.54) * mm, "end": v(-62.13, 838.13) * mm});
            skLineSegment(sketch, "E814", {"start": v(-62.13, 838.13) * mm, "end": v(-62.36, 837.74) * mm});
            skLineSegment(sketch, "E815", {"start": v(-62.36, 837.74) * mm, "end": v(-62.6, 837.35) * mm});
            skLineSegment(sketch, "E816", {"start": v(-62.6, 837.35) * mm, "end": v(-62.88, 836.98) * mm});
            skLineSegment(sketch, "E817", {"start": v(-62.88, 836.98) * mm, "end": v(-63.16, 836.62) * mm});
            skLineSegment(sketch, "E818", {"start": v(-63.16, 836.62) * mm, "end": v(-74.8, 823.63) * mm});
            skLineSegment(sketch, "E819", {"start": v(-63.16, 836.62) * mm, "end": v(-62.8, 837.04) * mm});
            skLineSegment(sketch, "E820", {"start": v(-62.8, 837.04) * mm, "end": v(-62.42, 837.44) * mm});
            skLineSegment(sketch, "E821", {"start": v(-62.42, 837.44) * mm, "end": v(-62.03, 837.82) * mm});
            skLineSegment(sketch, "E822", {"start": v(-62.03, 837.82) * mm, "end": v(-61.61, 838.17) * mm});
            skLineSegment(sketch, "E823", {"start": v(-61.61, 838.17) * mm, "end": v(-61.18, 838.5) * mm});
            skLineSegment(sketch, "E824", {"start": v(-61.18, 838.5) * mm, "end": v(-60.73, 838.81) * mm});
            skLineSegment(sketch, "E825", {"start": v(-60.73, 838.81) * mm, "end": v(-60.27, 839.1) * mm});
            skLineSegment(sketch, "E826", {"start": v(-60.27, 839.1) * mm, "end": v(-59.8, 839.37) * mm});
            skLineSegment(sketch, "E827", {"start": v(-59.8, 839.37) * mm, "end": v(-59.3, 839.6) * mm});
            skLineSegment(sketch, "E828", {"start": v(-59.3, 839.6) * mm, "end": v(-58.8, 839.82) * mm});
            skLineSegment(sketch, "E829", {"start": v(-58.8, 839.82) * mm, "end": v(-58.3, 840.01) * mm});
            skLineSegment(sketch, "E830", {"start": v(-58.3, 840.01) * mm, "end": v(-57.78, 840.18) * mm});
            skLineSegment(sketch, "E831", {"start": v(-57.78, 840.18) * mm, "end": v(-57.25, 840.31) * mm});
            skLineSegment(sketch, "E832", {"start": v(-57.25, 840.31) * mm, "end": v(-56.72, 840.43) * mm});
            skLineSegment(sketch, "E833", {"start": v(-56.72, 840.43) * mm, "end": v(-56.17, 840.51) * mm});
            skLineSegment(sketch, "E834", {"start": v(-56.17, 840.51) * mm, "end": v(-55.63, 840.57) * mm});
            skLineSegment(sketch, "E835", {"start": v(-55.63, 840.57) * mm, "end": v(-55.1, 840.6) * mm});
            skLineSegment(sketch, "E836", {"start": v(-55.1, 840.6) * mm, "end": v(-54.58, 840.6) * mm});
            skLineSegment(sketch, "E837", {"start": v(-54.58, 840.6) * mm, "end": v(-54.06, 840.56) * mm});
            skLineSegment(sketch, "E838", {"start": v(-54.06, 840.56) * mm, "end": v(-53.55, 840.5) * mm});
            skLineSegment(sketch, "E839", {"start": v(-53.55, 840.5) * mm, "end": v(-53.03, 840.43) * mm});
            skLineSegment(sketch, "E840", {"start": v(-53.03, 840.43) * mm, "end": v(-52.53, 840.32) * mm});
            skLineSegment(sketch, "E841", {"start": v(-52.53, 840.32) * mm, "end": v(-52.03, 840.2) * mm});
            skLineSegment(sketch, "E842", {"start": v(-52.03, 840.2) * mm, "end": v(-51.54, 840.03) * mm});
            skLineSegment(sketch, "E843", {"start": v(-51.54, 840.03) * mm, "end": v(-51.05, 839.85) * mm});
            skLineSegment(sketch, "E844", {"start": v(-51.05, 839.85) * mm, "end": v(-50.58, 839.65) * mm});
            skLineSegment(sketch, "E845", {"start": v(-50.58, 839.65) * mm, "end": v(-50.12, 839.42) * mm});
            skLineSegment(sketch, "E846", {"start": v(-50.12, 839.42) * mm, "end": v(-49.66, 839.17) * mm});
            skLineSegment(sketch, "E847", {"start": v(-49.66, 839.17) * mm, "end": v(-49.23, 838.9) * mm});
            skLineSegment(sketch, "E848", {"start": v(-49.23, 838.9) * mm, "end": v(-48.8, 838.6) * mm});
            skLineSegment(sketch, "E849", {"start": v(-48.8, 838.6) * mm, "end": v(-48.39, 838.27) * mm});
            skLineSegment(sketch, "E850", {"start": v(-48.39, 838.27) * mm, "end": v(-48, 837.93) * mm});
            skLineSegment(sketch, "E851", {"start": v(-48, 837.93) * mm, "end": v(-47.6, 837.58) * mm});
            skLineSegment(sketch, "E852", {"start": v(-47.6, 837.58) * mm, "end": v(-47.24, 837.21) * mm});
            skLineSegment(sketch, "E853", {"start": v(-47.24, 837.21) * mm, "end": v(-46.9, 836.83) * mm});
            skLineSegment(sketch, "E854", {"start": v(-46.9, 836.83) * mm, "end": v(-46.58, 836.43) * mm});
            skLineSegment(sketch, "E855", {"start": v(-46.58, 836.43) * mm, "end": v(-46.28, 836.02) * mm});
            skLineSegment(sketch, "E856", {"start": v(-46.28, 836.02) * mm, "end": v(-46, 835.59) * mm});
            skLineSegment(sketch, "E857", {"start": v(-46, 835.59) * mm, "end": v(-45.74, 835.15) * mm});
            skLineSegment(sketch, "E858", {"start": v(-45.74, 835.15) * mm, "end": v(-45.5, 834.7) * mm});
            skLineSegment(sketch, "E859", {"start": v(-45.5, 834.7) * mm, "end": v(-45.3, 834.23) * mm});
            skLineSegment(sketch, "E860", {"start": v(-45.3, 834.23) * mm, "end": v(-45.1, 833.75) * mm});
            skLineSegment(sketch, "E861", {"start": v(-45.1, 833.75) * mm, "end": v(-44.94, 833.27) * mm});
            skLineSegment(sketch, "E862", {"start": v(-44.94, 833.27) * mm, "end": v(-44.8, 832.78) * mm});
            skLineSegment(sketch, "E863", {"start": v(-44.8, 832.78) * mm, "end": v(-44.69, 832.28) * mm});
            skLineSegment(sketch, "E864", {"start": v(-44.69, 832.28) * mm, "end": v(-44.6, 831.77) * mm});
            skLineSegment(sketch, "E865", {"start": v(-44.6, 831.77) * mm, "end": v(-44.53, 831.26) * mm});
            skLineSegment(sketch, "E866", {"start": v(-44.53, 831.26) * mm, "end": v(-44.5, 830.74) * mm});
            skLineSegment(sketch, "E867", {"start": v(-44.5, 830.74) * mm, "end": v(-44.47, 830.23) * mm});
            skLineSegment(sketch, "E868", {"start": v(-44.47, 830.23) * mm, "end": v(-44.46, 829.73) * mm});
            skLineSegment(sketch, "E869", {"start": v(-44.46, 829.73) * mm, "end": v(-44.49, 829.22) * mm});
            skLineSegment(sketch, "E870", {"start": v(-44.49, 829.22) * mm, "end": v(-44.53, 828.72) * mm});
            skLineSegment(sketch, "E871", {"start": v(-44.53, 828.72) * mm, "end": v(-44.6, 828.22) * mm});
            skLineSegment(sketch, "E872", {"start": v(-44.6, 828.22) * mm, "end": v(-44.7, 827.73) * mm});
            skLineSegment(sketch, "E873", {"start": v(-44.7, 827.73) * mm, "end": v(-44.83, 827.24) * mm});
            skLineSegment(sketch, "E874", {"start": v(-44.83, 827.24) * mm, "end": v(-44.98, 826.76) * mm});
            skLineSegment(sketch, "E875", {"start": v(-44.98, 826.76) * mm, "end": v(-45.15, 826.3) * mm});
            skLineSegment(sketch, "E876", {"start": v(-45.15, 826.3) * mm, "end": v(-45.34, 825.83) * mm});
            skLineSegment(sketch, "E877", {"start": v(-45.34, 825.83) * mm, "end": v(-45.56, 825.38) * mm});
            skLineSegment(sketch, "E878", {"start": v(-45.56, 825.38) * mm, "end": v(-45.8, 824.93) * mm});
            skLineSegment(sketch, "E879", {"start": v(-45.8, 824.93) * mm, "end": v(-46.07, 824.5) * mm});
            skLineSegment(sketch, "E880", {"start": v(-46.07, 824.5) * mm, "end": v(-46.35, 824.09) * mm});
            skLineSegment(sketch, "E881", {"start": v(-46.35, 824.09) * mm, "end": v(-46.66, 823.69) * mm});
            skLineSegment(sketch, "E882", {"start": v(-46.66, 823.69) * mm, "end": v(-46.99, 823.3) * mm});
            skLineSegment(sketch, "E883", {"start": v(-46.99, 823.3) * mm, "end": v(-59.2, 809.66) * mm});
            skArc(sketch, "E884", {"start": v(-560.88, -1165.36) * mm, "mid": v(-563, -1166.23) * mm, "end": v(-563.88, -1168.36) * mm});
            skArc(sketch, "E885", {"start": v(-563.88, -1168.36) * mm, "mid": v(-563, -1170.48) * mm, "end": v(-560.88, -1171.36) * mm});
            skArc(sketch, "E886", {"start": v(-560.88, -1171.36) * mm, "mid": v(-558.76, -1170.48) * mm, "end": v(-557.88, -1168.36) * mm});
            skArc(sketch, "E887", {"start": v(-557.88, -1168.36) * mm, "mid": v(-558.76, -1166.23) * mm, "end": v(-560.88, -1165.36) * mm});
            skArc(sketch, "E888", {"start": v(27.35, -1157.97) * mm, "mid": v(25.23, -1158.85) * mm, "end": v(24.35, -1160.97) * mm});
            skArc(sketch, "E889", {"start": v(24.35, -1160.97) * mm, "mid": v(25.23, -1163.1) * mm, "end": v(27.35, -1163.97) * mm});
            skArc(sketch, "E890", {"start": v(27.35, -1163.97) * mm, "mid": v(29.47, -1163.1) * mm, "end": v(30.35, -1160.97) * mm});
            skArc(sketch, "E891", {"start": v(30.35, -1160.97) * mm, "mid": v(29.47, -1158.85) * mm, "end": v(27.35, -1157.97) * mm});
            skArc(sketch, "E892", {"start": v(587.54, -1183.53) * mm, "mid": v(585.42, -1184.41) * mm, "end": v(584.54, -1186.53) * mm});
            skArc(sketch, "E893", {"start": v(584.54, -1186.53) * mm, "mid": v(585.42, -1188.65) * mm, "end": v(587.54, -1189.53) * mm});
            skArc(sketch, "E894", {"start": v(587.54, -1189.53) * mm, "mid": v(589.66, -1188.65) * mm, "end": v(590.54, -1186.53) * mm});
            skArc(sketch, "E895", {"start": v(590.54, -1186.53) * mm, "mid": v(589.66, -1184.41) * mm, "end": v(587.54, -1183.53) * mm});
            skArc(sketch, "E896", {"start": v(-564.8, -586.08) * mm, "mid": v(-566.92, -586.96) * mm, "end": v(-567.8, -589.08) * mm});
            skArc(sketch, "E897", {"start": v(-567.8, -589.08) * mm, "mid": v(-566.92, -591.2) * mm, "end": v(-564.8, -592.08) * mm});
            skArc(sketch, "E898", {"start": v(-564.8, -592.08) * mm, "mid": v(-562.67, -591.2) * mm, "end": v(-561.8, -589.08) * mm});
            skArc(sketch, "E899", {"start": v(-561.8, -589.08) * mm, "mid": v(-562.67, -586.96) * mm, "end": v(-564.8, -586.08) * mm});
            skArc(sketch, "E900", {"start": v(-209.08, -480.32) * mm, "mid": v(-211.2, -481.2) * mm, "end": v(-212.08, -483.32) * mm});
            skArc(sketch, "E901", {"start": v(-212.08, -483.32) * mm, "mid": v(-211.2, -485.45) * mm, "end": v(-209.08, -486.32) * mm});
            skArc(sketch, "E902", {"start": v(-209.08, -486.32) * mm, "mid": v(-206.96, -485.45) * mm, "end": v(-206.08, -483.32) * mm});
            skArc(sketch, "E903", {"start": v(-206.08, -483.32) * mm, "mid": v(-206.96, -481.2) * mm, "end": v(-209.08, -480.32) * mm});
            skArc(sketch, "E904", {"start": v(103.38, -684.62) * mm, "mid": v(101.26, -685.5) * mm, "end": v(100.38, -687.62) * mm});
            skArc(sketch, "E905", {"start": v(100.38, -687.62) * mm, "mid": v(101.26, -689.74) * mm, "end": v(103.38, -690.62) * mm});
            skArc(sketch, "E906", {"start": v(103.38, -690.62) * mm, "mid": v(105.5, -689.74) * mm, "end": v(106.38, -687.62) * mm});
            skArc(sketch, "E907", {"start": v(106.38, -687.62) * mm, "mid": v(105.5, -685.5) * mm, "end": v(103.38, -684.62) * mm});
            skArc(sketch, "E908", {"start": v(552.84, -297.66) * mm, "mid": v(550.71, -298.54) * mm, "end": v(549.84, -300.66) * mm});
            skArc(sketch, "E909", {"start": v(549.84, -300.66) * mm, "mid": v(550.71, -302.78) * mm, "end": v(552.84, -303.66) * mm});
            skArc(sketch, "E910", {"start": v(552.84, -303.66) * mm, "mid": v(554.96, -302.78) * mm, "end": v(555.84, -300.66) * mm});
            skArc(sketch, "E911", {"start": v(555.84, -300.66) * mm, "mid": v(554.96, -298.54) * mm, "end": v(552.84, -297.66) * mm});
            skArc(sketch, "E912", {"start": v(194.71, 41.24) * mm, "mid": v(192.6, 40.36) * mm, "end": v(191.71, 38.24) * mm});
            skArc(sketch, "E913", {"start": v(191.71, 38.24) * mm, "mid": v(192.6, 36.12) * mm, "end": v(194.71, 35.24) * mm});
            skArc(sketch, "E914", {"start": v(194.71, 35.24) * mm, "mid": v(196.83, 36.12) * mm, "end": v(197.71, 38.24) * mm});
            skArc(sketch, "E915", {"start": v(197.71, 38.24) * mm, "mid": v(196.83, 40.36) * mm, "end": v(194.71, 41.24) * mm});
            skArc(sketch, "E916", {"start": v(-132.16, 26.82) * mm, "mid": v(-134.29, 25.94) * mm, "end": v(-135.16, 23.82) * mm});
            skArc(sketch, "E917", {"start": v(-135.16, 23.82) * mm, "mid": v(-134.29, 21.7) * mm, "end": v(-132.16, 20.82) * mm});
            skArc(sketch, "E918", {"start": v(-132.16, 20.82) * mm, "mid": v(-130.04, 21.7) * mm, "end": v(-129.16, 23.82) * mm});
            skArc(sketch, "E919", {"start": v(-129.16, 23.82) * mm, "mid": v(-130.04, 25.94) * mm, "end": v(-132.16, 26.82) * mm});
            skArc(sketch, "E920", {"start": v(-545.57, 55.66) * mm, "mid": v(-547.69, 54.78) * mm, "end": v(-548.57, 52.66) * mm});
            skArc(sketch, "E921", {"start": v(-548.57, 52.66) * mm, "mid": v(-547.69, 50.54) * mm, "end": v(-545.57, 49.66) * mm});
            skArc(sketch, "E922", {"start": v(-545.57, 49.66) * mm, "mid": v(-543.45, 50.54) * mm, "end": v(-542.57, 52.66) * mm});
            skArc(sketch, "E923", {"start": v(-542.57, 52.66) * mm, "mid": v(-543.45, 54.78) * mm, "end": v(-545.57, 55.66) * mm});
            skArc(sketch, "E924", {"start": v(550.43, 435.41) * mm, "mid": v(548.31, 434.53) * mm, "end": v(547.43, 432.41) * mm});
            skArc(sketch, "E925", {"start": v(547.43, 432.41) * mm, "mid": v(548.31, 430.3) * mm, "end": v(550.43, 429.41) * mm});
            skArc(sketch, "E926", {"start": v(550.43, 429.41) * mm, "mid": v(552.55, 430.3) * mm, "end": v(553.43, 432.41) * mm});
            skArc(sketch, "E927", {"start": v(553.43, 432.41) * mm, "mid": v(552.55, 434.53) * mm, "end": v(550.43, 435.41) * mm});
            skArc(sketch, "E928", {"start": v(16.85, 500.3) * mm, "mid": v(14.73, 499.43) * mm, "end": v(13.85, 497.3) * mm});
            skArc(sketch, "E929", {"start": v(13.85, 497.3) * mm, "mid": v(14.73, 495.19) * mm, "end": v(16.85, 494.3) * mm});
            skArc(sketch, "E930", {"start": v(16.85, 494.3) * mm, "mid": v(18.97, 495.19) * mm, "end": v(19.85, 497.3) * mm});
            skArc(sketch, "E931", {"start": v(19.85, 497.3) * mm, "mid": v(18.97, 499.43) * mm, "end": v(16.85, 500.3) * mm});
            skArc(sketch, "E932", {"start": v(-396.55, 618.08) * mm, "mid": v(-398.67, 617.2) * mm, "end": v(-399.55, 615.08) * mm});
            skArc(sketch, "E933", {"start": v(-399.55, 615.08) * mm, "mid": v(-398.67, 612.96) * mm, "end": v(-396.55, 612.08) * mm});
            skArc(sketch, "E934", {"start": v(-396.55, 612.08) * mm, "mid": v(-394.43, 612.96) * mm, "end": v(-393.55, 615.08) * mm});
            skArc(sketch, "E935", {"start": v(-393.55, 615.08) * mm, "mid": v(-394.43, 617.2) * mm, "end": v(-396.55, 618.08) * mm});
            skArc(sketch, "E936", {"start": v(343.73, 771.9) * mm, "mid": v(341.6, 771.03) * mm, "end": v(340.73, 768.9) * mm});
            skArc(sketch, "E937", {"start": v(340.73, 768.9) * mm, "mid": v(341.6, 766.78) * mm, "end": v(343.73, 765.9) * mm});
            skArc(sketch, "E938", {"start": v(343.73, 765.9) * mm, "mid": v(345.85, 766.78) * mm, "end": v(346.73, 768.9) * mm});
            skArc(sketch, "E939", {"start": v(346.73, 768.9) * mm, "mid": v(345.85, 771.03) * mm, "end": v(343.73, 771.9) * mm});
            skArc(sketch, "E940", {"start": v(572.06, 1168.48) * mm, "mid": v(569.94, 1167.6) * mm, "end": v(569.06, 1165.48) * mm});
            skArc(sketch, "E941", {"start": v(569.06, 1165.48) * mm, "mid": v(569.94, 1163.36) * mm, "end": v(572.06, 1162.48) * mm});
            skArc(sketch, "E942", {"start": v(572.06, 1162.48) * mm, "mid": v(574.19, 1163.36) * mm, "end": v(575.06, 1165.48) * mm});
            skArc(sketch, "E943", {"start": v(575.06, 1165.48) * mm, "mid": v(574.19, 1167.6) * mm, "end": v(572.06, 1168.48) * mm});
            skArc(sketch, "E944", {"start": v(-124.95, 1031.48) * mm, "mid": v(-127.08, 1030.6) * mm, "end": v(-127.95, 1028.48) * mm});
            skArc(sketch, "E945", {"start": v(-127.95, 1028.48) * mm, "mid": v(-127.08, 1026.36) * mm, "end": v(-124.95, 1025.48) * mm});
            skArc(sketch, "E946", {"start": v(-124.95, 1025.48) * mm, "mid": v(-122.83, 1026.36) * mm, "end": v(-121.95, 1028.48) * mm});
            skArc(sketch, "E947", {"start": v(-121.95, 1028.48) * mm, "mid": v(-122.83, 1030.6) * mm, "end": v(-124.95, 1031.48) * mm});
            skArc(sketch, "E948", {"start": v(-579.42, 1143.76) * mm, "mid": v(-581.55, 1142.88) * mm, "end": v(-582.42, 1140.76) * mm});
            skArc(sketch, "E949", {"start": v(-582.42, 1140.76) * mm, "mid": v(-581.55, 1138.63) * mm, "end": v(-579.42, 1137.76) * mm});
            skArc(sketch, "E950", {"start": v(-579.42, 1137.76) * mm, "mid": v(-577.3, 1138.63) * mm, "end": v(-576.42, 1140.76) * mm});
            skArc(sketch, "E951", {"start": v(-576.42, 1140.76) * mm, "mid": v(-577.3, 1142.88) * mm, "end": v(-579.42, 1143.76) * mm});
            skSolve(sketch);
        }
        {
            var Q0;
            Q0=makeQuery(id+"F0.imprint","IMPRINT",FACE,{"disambiguationData":[TD([[makeQuery(id+"F0.imprint","IMPRINT",EDGE,{"derivedFrom":sQuery(id+"F0.wireOp",EDGE,"E280")}),1.0]])]});
            var Q1;
            {var subQ0=sQuery(id+"F0.wireOp",EDGE,"E753");Q1=makeQuery(id+"F0.imprint","IMPRINT",FACE,{"disambiguationData":[TD([[makeQuery(id+"F0.imprint","IMPRINT",EDGE,{"derivedFrom":subQ0}),-1.0]])]});}
            var Q2;
            {var subQ2=sQuery(id+"F0.wireOp",EDGE,"E818");Q2=makeQuery(id+"F0.imprint","IMPRINT",FACE,{"disambiguationData":[TD([[makeQuery(id+"F0.imprint","IMPRINT",EDGE,{"derivedFrom":subQ2}),1.0]])]});}
            extrude(context, id + "F1", {"entities" : qUnion([Q0, Q1, Q2]), "depth" : 18 * mm});
        }
        {
            var Q0;
            Q0=makeQuery(id+"F0.imprint","IMPRINT",FACE,{"disambiguationData":[TD([[makeQuery(id+"F0.imprint","IMPRINT",EDGE,{"derivedFrom":sQuery(id+"F0.wireOp",EDGE,"E160")}),1.0]])]});
            var Q1;
            Q1=makeQuery(id+"F0.imprint","IMPRINT",FACE,{"disambiguationData":[TD([[makeQuery(id+"F0.imprint","IMPRINT",EDGE,{"derivedFrom":sQuery(id+"F0.wireOp",EDGE,"E543")}),-1.0]])]});
            extrude(context, id + "F2", {"entities" : qUnion([Q0, Q1]), "depth" : 25 * mm});
        }
        {
            var Q0;
            Q0=makeQuery(id+"F0.imprint","IMPRINT",FACE,{"disambiguationData":[TD([[makeQuery(id+"F0.imprint","IMPRINT",EDGE,{"derivedFrom":sQuery(id+"F0.wireOp",EDGE,"E160")}),1.0]])]});
            var Q1;
            Q1=makeQuery(id+"F0.imprint","IMPRINT",FACE,{"disambiguationData":[TD([[makeQuery(id+"F0.imprint","IMPRINT",EDGE,{"derivedFrom":sQuery(id+"F0.wireOp",EDGE,"E543")}),-1.0]])]});
            extrude(context, id + "F3", {"entities" : qUnion([Q0, Q1]), "depth" : 18 * mm});
        }
        {
            var Q0;
            Q0=makeQuery(id+"F0.imprint","IMPRINT",FACE,{"disambiguationData":[TD([[makeQuery(id+"F0.imprint","IMPRINT",EDGE,{"derivedFrom":sQuery(id+"F0.wireOp",EDGE,"E160")}),1.0]])]});
            var Q1;
            Q1=makeQuery(id+"F0.imprint","IMPRINT",FACE,{"disambiguationData":[TD([[makeQuery(id+"F0.imprint","IMPRINT",EDGE,{"derivedFrom":sQuery(id+"F0.wireOp",EDGE,"E543")}),-1.0]])]});
            extrude(context, id + "F4", {"entities" : qUnion([Q0, Q1]), "depth" : 25 * mm});
        }
    });
